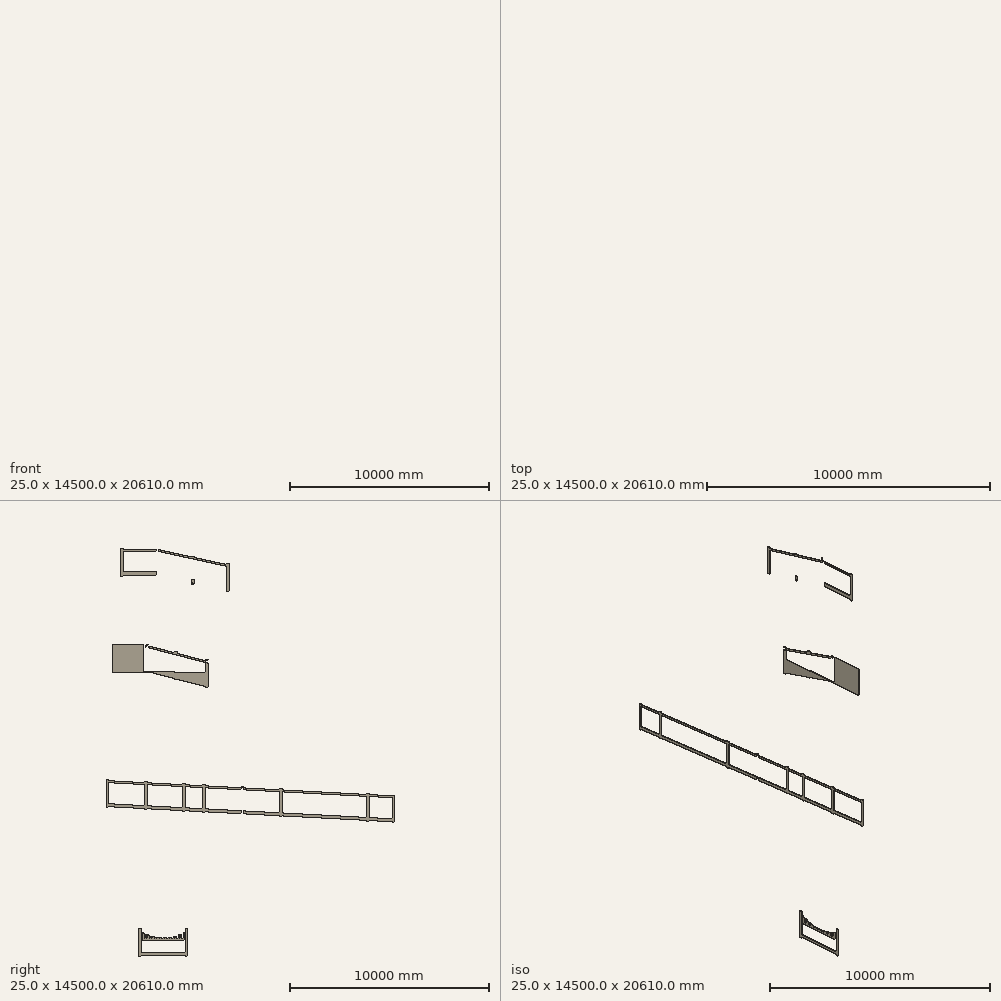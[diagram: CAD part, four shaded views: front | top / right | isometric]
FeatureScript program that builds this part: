
annotation { "Feature Type Name" : "Feature", "Feature Type Description" : "" }
export const myFeature = defineFeature(function(context is Context, id is Id, definition is map)
    precondition{}
    {
        {
            var Q0;
            Q0=qCreatedBy(makeId("Right.planeOp"),FACE);
            var sketch = newSketch(context, id + "F0", { "sketchPlane" : qUnion([Q0])});
            skLineSegment(sketch, "E0", {"start": v(-1036.7, 0) * mm, "end": v(-909.7, 0) * mm});
            skLineSegment(sketch, "E1.top", {"start": v(-1036.7, 1400) * mm, "end": v(-909.7, 1400) * mm});
            skLineSegment(sketch, "E1.left", {"start": v(-1036.7, 0) * mm, "end": v(-1036.7, 1400) * mm});
            skLineSegment(sketch, "E1.right", {"start": v(-909.7, 0) * mm, "end": v(-909.7, 1400) * mm});
            skLineSegment(sketch, "E2", {"start": v(4423.3, 650) * mm, "end": v(4423.3, -750) * mm});
            skLineSegment(sketch, "E3", {"start": v(4423.3, -750) * mm, "end": v(4296.3, -750) * mm});
            skLineSegment(sketch, "E4", {"start": v(4296.3, -750) * mm, "end": v(4296.3, 650) * mm});
            skLineSegment(sketch, "E5", {"start": v(4296.3, 650) * mm, "end": v(4423.3, 650) * mm});
            skPoint(sketch, "E6.orphan", {"position": v(4423.3, 1400) * mm});
            skPoint(sketch, "E7.orphan", {"position": v(8746.3, 0) * mm});
            skLineSegment(sketch, "E8", {"start": v(4296.3, -700) * mm, "end": v(4296.3, -515.03) * mm});
            skLineSegment(sketch, "E9.trimOffspring", {"start": v(4296.3, 0) * mm, "end": v(4423.3, 0) * mm});
            skLineSegment(sketch, "E10", {"start": v(740.8, 1183.99) * mm, "end": v(740.8, 0) * mm});
            skLineSegment(sketch, "E11", {"start": v(867.8, 0) * mm, "end": v(867.8, 1183.99) * mm});
            skLineSegment(sketch, "E12", {"start": v(2518.3, 1009.98) * mm, "end": v(2518.3, -390.02) * mm});
            skLineSegment(sketch, "E13", {"start": v(2518.3, -390.02) * mm, "end": v(2645.3, -390.02) * mm});
            skLineSegment(sketch, "E14", {"start": v(2645.3, -390.02) * mm, "end": v(2645.3, 1009.98) * mm});
            skLineSegment(sketch, "E15", {"start": v(2645.3, 1009.98) * mm, "end": v(2518.3, 1009.98) * mm});
            skLineSegment(sketch, "E16", {"start": v(-1450.3, -4815.22) * mm, "end": v(3379.7, -4815.22) * mm});
            skLineSegment(sketch, "E17", {"start": v(-1450.3, -3415.22) * mm, "end": v(-1450.3, -4815.22) * mm});
            skLineSegment(sketch, "E18", {"start": v(-1295.9, -4815.22) * mm, "end": v(-1295.9, -3415.22) * mm});
            skLineSegment(sketch, "E19", {"start": v(-1295.9, -3415.22) * mm, "end": v(-1450.3, -3415.22) * mm});
            skLineSegment(sketch, "E20.1.0.0", {"start": v(265.98, -4815.22) * mm, "end": v(265.98, -3415.7) * mm});
            skLineSegment(sketch, "E20.1.0.1", {"start": v(109.7, -3415.7) * mm, "end": v(109.7, -4815.22) * mm});
            skLineSegment(sketch, "E20.1.0.2", {"start": v(265.98, -3415.7) * mm, "end": v(109.7, -3415.7) * mm});
            skLineSegment(sketch, "E20.2.0.0", {"start": v(1824.1, -5179) * mm, "end": v(1824.1, -3779) * mm});
            skLineSegment(sketch, "E20.2.0.1", {"start": v(1671.6, -3779) * mm, "end": v(1671.6, -5179) * mm});
            skLineSegment(sketch, "E20.2.0.2", {"start": v(1824.1, -3407.94) * mm, "end": v(1671.6, -3407.94) * mm});
            skLineSegment(sketch, "E20.3.0.0", {"start": v(3384.1, -5585.22) * mm, "end": v(3384.1, -4185.22) * mm});
            skLineSegment(sketch, "E20.3.0.1", {"start": v(3229.7, -4185.22) * mm, "end": v(3229.7, -5585.22) * mm});
            skLineSegment(sketch, "E20.3.0.2", {"start": v(3384.1, -3415.22) * mm, "end": v(3229.7, -3415.22) * mm});
            skLineSegment(sketch, "E21", {"start": v(3229.7, -5585.22) * mm, "end": v(3384.1, -5585.22) * mm});
            skLineSegment(sketch, "E22", {"start": v(-1295.9, -3415.22) * mm, "end": v(5420.8, -3415.22) * mm});
            skLineSegment(sketch, "E23", {"start": v(3384.1, -4185.22) * mm, "end": v(3229.7, -4185.22) * mm});
            skLineSegment(sketch, "E24", {"start": v(1671.6, -3779) * mm, "end": v(1824.1, -3779) * mm});
            skLineSegment(sketch, "E25", {"start": v(109.7, -3465.7) * mm, "end": v(265.98, -3465.7) * mm});
            skLineSegment(sketch, "E26", {"start": v(3229.7, -4235.22) * mm, "end": v(3384.1, -4235.22) * mm});
            skLineSegment(sketch, "E27", {"start": v(-1450.3, -3465.22) * mm, "end": v(-1295.9, -3465.22) * mm});
            skPoint(sketch, "E28.orphan", {"position": v(0, -3465.7) * mm});
            skLineSegment(sketch, "E29", {"start": v(265.98, -3465.7) * mm, "end": v(3229.7, -4235.22) * mm});
            skLineSegment(sketch, "E30", {"start": v(1671.6, -5179) * mm, "end": v(1824.1, -5179) * mm});
            skLineSegment(sketch, "E31", {"start": v(-1450.3, -4765.22) * mm, "end": v(3379.7, -4765.22) * mm});
            skLineSegment(sketch, "E32", {"start": v(265.98, -4765.22) * mm, "end": v(3229.7, -5535.22) * mm});
            skLineSegment(sketch, "E33", {"start": v(740.8, 1183.99) * mm, "end": v(740.8, 1400) * mm});
            skLineSegment(sketch, "E34", {"start": v(740.8, 1400) * mm, "end": v(867.8, 1400) * mm});
            skLineSegment(sketch, "E35", {"start": v(867.8, 1400) * mm, "end": v(867.8, 1183.99) * mm});
            skLineSegment(sketch, "E36", {"start": v(-909.7, 1350) * mm, "end": v(740.8, 1350) * mm});
            skLineSegment(sketch, "E37", {"start": v(740.8, 1350) * mm, "end": v(740.8, 1261.25) * mm});
            skLineSegment(sketch, "E38", {"start": v(740.8, 1261.25) * mm, "end": v(-909.7, 1261.25) * mm});
            skLineSegment(sketch, "E39", {"start": v(867.8, 1350) * mm, "end": v(4296.3, 600) * mm});
            skLineSegment(sketch, "E40", {"start": v(4296.3, 511.25) * mm, "end": v(867.8, 1261.25) * mm});
            skLineSegment(sketch, "E41", {"start": v(-909.7, 234.97) * mm, "end": v(740.8, 234.97) * mm});
            skLineSegment(sketch, "E42", {"start": v(740.8, 234.97) * mm, "end": v(740.8, 50) * mm});
            skLineSegment(sketch, "E43", {"start": v(740.8, 50) * mm, "end": v(-909.7, 50) * mm});
            skLineSegment(sketch, "E44", {"start": v(4296.3, -700) * mm, "end": v(867.8, 50) * mm});
            skLineSegment(sketch, "E45", {"start": v(867.8, 50) * mm, "end": v(867.8, 234.97) * mm});
            skLineSegment(sketch, "E46", {"start": v(867.8, 234.97) * mm, "end": v(4296.3, -515.03) * mm});
            skLineSegment(sketch, "E47", {"start": v(740.8, 0) * mm, "end": v(867.8, 0) * mm});
            skLineSegment(sketch, "E48.trimOffspring", {"start": v(867.8, 1400) * mm, "end": v(740.8, 1400) * mm});
            skPoint(sketch, "E49.start.orphan", {"position": v(5203.57, 1400) * mm});
            skPoint(sketch, "E50.trimOffspring.end.orphan", {"position": v(2518.3, 1400) * mm});
            skLineSegment(sketch, "E51", {"start": v(936.62, 219.92) * mm, "end": v(936.62, 1511.5) * mm});
            skLineSegment(sketch, "E52", {"start": v(936.62, 1511.5) * mm, "end": v(974.62, 1511.5) * mm});
            skLineSegment(sketch, "E53", {"start": v(974.62, 1511.5) * mm, "end": v(974.62, 127.15) * mm});
            skLineSegment(sketch, "E54", {"start": v(974.62, 127.15) * mm, "end": v(936.62, 127.15) * mm});
            skLineSegment(sketch, "E55", {"start": v(936.62, 127.15) * mm, "end": v(936.62, 219.92) * mm});
            skLineSegment(sketch, "E56", {"start": v(964.44, 213.83) * mm, "end": v(986.75, 208.95) * mm});
            skLineSegment(sketch, "E57", {"start": v(867.8, 234.97) * mm, "end": v(6462.55, 234.97) * mm});
            skLineSegment(sketch, "E58", {"start": v(2645.3, -153.86) * mm, "end": v(6982.64, -153.86) * mm});
            skLineSegment(sketch, "E59", {"start": v(-1767.52, -11612.14) * mm, "end": v(-1640.52, -11612.14) * mm});
            skLineSegment(sketch, "E60", {"start": v(12732.48, -12382.14) * mm, "end": v(12732.48, -11612.14) * mm});
            skLineSegment(sketch, "E61", {"start": v(12732.48, -12382.14) * mm, "end": v(12605.48, -12375.4) * mm});
            skLineSegment(sketch, "E62", {"start": v(-1767.52, -11612.14) * mm, "end": v(-1767.52, -10212.14) * mm});
            skLineSegment(sketch, "E63", {"start": v(-1767.52, -10212.14) * mm, "end": v(-1640.52, -10212.14) * mm});
            skLineSegment(sketch, "E64", {"start": v(-1640.52, -10212.14) * mm, "end": v(-1640.52, -10262.14) * mm});
            skLineSegment(sketch, "E65", {"start": v(-1640.52, -11568.81) * mm, "end": v(162.48, -11664.56) * mm});
            skLineSegment(sketch, "E66", {"start": v(12732.48, -12382.14) * mm, "end": v(12732.48, -10982.14) * mm});
            skLineSegment(sketch, "E67", {"start": v(12732.48, -10982.14) * mm, "end": v(12605.48, -10982.14) * mm});
            skLineSegment(sketch, "E68", {"start": v(12605.48, -10982.14) * mm, "end": v(12605.48, -11018.65) * mm});
            skLineSegment(sketch, "E69", {"start": v(-1640.52, -10262.14) * mm, "end": v(162.48, -10357.88) * mm});
            skLineSegment(sketch, "E70.bottom", {"start": v(162.48, -10314.63) * mm, "end": v(289.48, -10314.63) * mm});
            skLineSegment(sketch, "E70.top", {"start": v(162.48, -11714.63) * mm, "end": v(289.48, -11714.63) * mm});
            skLineSegment(sketch, "E70.left", {"start": v(162.48, -10314.63) * mm, "end": v(162.48, -11714.63) * mm});
            skLineSegment(sketch, "E70.right", {"start": v(289.48, -10314.63) * mm, "end": v(289.48, -11714.63) * mm});
            skLineSegment(sketch, "E71.2.0.0", {"start": v(11312.48, -10896.15) * mm, "end": v(11312.48, -12296.15) * mm});
            skLineSegment(sketch, "E71.2.0.1", {"start": v(11439.48, -10896.15) * mm, "end": v(11439.48, -12296.15) * mm});
            skLineSegment(sketch, "E71.2.0.2", {"start": v(11312.48, -12296.15) * mm, "end": v(11439.48, -12296.15) * mm});
            skLineSegment(sketch, "E71.2.0.3", {"start": v(11312.48, -10896.15) * mm, "end": v(11439.48, -10896.15) * mm});
            skLineSegment(sketch, "E72.bottom", {"start": v(2075.48, -10401.68) * mm, "end": v(2202.48, -10401.68) * mm});
            skLineSegment(sketch, "E72.top", {"start": v(2075.48, -11801.68) * mm, "end": v(2202.48, -11801.68) * mm});
            skLineSegment(sketch, "E72.left", {"start": v(2075.48, -10401.68) * mm, "end": v(2075.48, -11801.68) * mm});
            skLineSegment(sketch, "E72.right", {"start": v(2202.48, -10401.68) * mm, "end": v(2202.48, -11801.68) * mm});
            skLineSegment(sketch, "E73.bottom", {"start": v(3082.48, -10447.1) * mm, "end": v(3209.48, -10447.1) * mm});
            skLineSegment(sketch, "E73.top", {"start": v(3082.48, -11847.1) * mm, "end": v(3209.48, -11847.1) * mm});
            skLineSegment(sketch, "E73.left", {"start": v(3082.48, -10447.1) * mm, "end": v(3082.48, -11847.1) * mm});
            skLineSegment(sketch, "E73.right", {"start": v(3209.48, -10447.1) * mm, "end": v(3209.48, -11847.1) * mm});
            skLineSegment(sketch, "E74.bottom", {"start": v(6942.48, -10674.67) * mm, "end": v(7069.48, -10674.67) * mm});
            skLineSegment(sketch, "E74.top", {"start": v(6942.48, -12074.67) * mm, "end": v(7069.48, -12074.67) * mm});
            skLineSegment(sketch, "E74.left", {"start": v(6942.48, -10674.67) * mm, "end": v(6942.48, -12074.67) * mm});
            skLineSegment(sketch, "E74.right", {"start": v(7069.48, -10674.67) * mm, "end": v(7069.48, -12074.67) * mm});
            skLineSegment(sketch, "E75.bottom", {"start": v(5012.48, -10552.15) * mm, "end": v(5139.48, -10552.15) * mm});
            skLineSegment(sketch, "E75.top", {"start": v(5012.48, -11952.15) * mm, "end": v(5139.48, -11952.15) * mm});
            skLineSegment(sketch, "E75.left", {"start": v(5012.48, -10552.15) * mm, "end": v(5012.48, -11952.15) * mm});
            skLineSegment(sketch, "E75.right", {"start": v(5139.48, -10552.15) * mm, "end": v(5139.48, -11952.15) * mm});
            skLineSegment(sketch, "E76", {"start": v(-1640.52, -10361.17) * mm, "end": v(162.48, -10456.91) * mm});
            skLineSegment(sketch, "E77", {"start": v(-1640.52, -11418.6) * mm, "end": v(162.48, -11514.35) * mm});
            skLineSegment(sketch, "E78.trimOffspring", {"start": v(-1640.52, -11618.88) * mm, "end": v(-1767.52, -11612.14) * mm});
            skLineSegment(sketch, "E79.trimOffspring", {"start": v(12605.48, -12325.32) * mm, "end": v(12605.48, -12375.4) * mm});
            skLineSegment(sketch, "E80.trimOffspring", {"start": v(12605.48, -11117.68) * mm, "end": v(12605.48, -12175.11) * mm});
            skLineSegment(sketch, "E81.trimOffspring", {"start": v(11439.48, -12263.4) * mm, "end": v(12605.48, -12325.32) * mm});
            skLineSegment(sketch, "E82.trimOffspring", {"start": v(11439.48, -12113.2) * mm, "end": v(12605.48, -12175.11) * mm});
            skLineSegment(sketch, "E83.trimOffspring", {"start": v(11439.48, -10956.73) * mm, "end": v(12605.48, -11018.65) * mm});
            skLineSegment(sketch, "E84.trimOffspring", {"start": v(11439.48, -11055.76) * mm, "end": v(12605.48, -11117.68) * mm});
            skLineSegment(sketch, "E85.trimOffspring", {"start": v(7069.48, -10823.7) * mm, "end": v(11312.48, -11049.02) * mm});
            skLineSegment(sketch, "E86.trimOffspring", {"start": v(7069.48, -10724.67) * mm, "end": v(11312.48, -10949.99) * mm});
            skLineSegment(sketch, "E87.trimOffspring", {"start": v(7069.48, -11881.13) * mm, "end": v(11312.48, -12106.45) * mm});
            skLineSegment(sketch, "E88.trimOffspring", {"start": v(7069.48, -12031.34) * mm, "end": v(11312.48, -12256.66) * mm});
            skLineSegment(sketch, "E89.trimOffspring", {"start": v(5139.48, -11928.85) * mm, "end": v(6942.48, -12024.6) * mm});
            skLineSegment(sketch, "E90.trimOffspring", {"start": v(5139.48, -11778.64) * mm, "end": v(6942.48, -11874.39) * mm});
            skLineSegment(sketch, "E91.trimOffspring", {"start": v(5139.48, -10721.21) * mm, "end": v(6942.48, -10816.96) * mm});
            skLineSegment(sketch, "E92.trimOffspring", {"start": v(5139.48, -10622.18) * mm, "end": v(6942.48, -10717.93) * mm});
            skLineSegment(sketch, "E93.trimOffspring", {"start": v(2202.48, -10466.22) * mm, "end": v(5012.48, -10615.44) * mm});
            skLineSegment(sketch, "E94.trimOffspring", {"start": v(2202.48, -10565.25) * mm, "end": v(5012.48, -10714.47) * mm});
            skLineSegment(sketch, "E95.trimOffspring", {"start": v(2202.48, -11622.68) * mm, "end": v(5012.48, -11771.9) * mm});
            skLineSegment(sketch, "E96.trimOffspring", {"start": v(2202.48, -11772.89) * mm, "end": v(5012.48, -11922.1) * mm});
            skLineSegment(sketch, "E97.trimOffspring", {"start": v(289.48, -11671.3) * mm, "end": v(2075.48, -11766.14) * mm});
            skLineSegment(sketch, "E98.trimOffspring", {"start": v(289.48, -11521.1) * mm, "end": v(2075.48, -11615.93) * mm});
            skLineSegment(sketch, "E99.trimOffspring", {"start": v(289.48, -10364.63) * mm, "end": v(2075.48, -10459.47) * mm});
            skLineSegment(sketch, "E100.trimOffspring", {"start": v(289.48, -10463.66) * mm, "end": v(2075.48, -10558.5) * mm});
            skLineSegment(sketch, "E101.trimOffspring", {"start": v(-1640.52, -10361.17) * mm, "end": v(-1640.52, -11418.6) * mm});
            skLineSegment(sketch, "E102.trimOffspring", {"start": v(-1640.52, -11568.81) * mm, "end": v(-1640.52, -11618.88) * mm});
            skLineSegment(sketch, "E103.left", {"start": v(0, -17698.55) * mm, "end": v(0, -19098.55) * mm});
            skLineSegment(sketch, "E103.right", {"start": v(2213, -17698.55) * mm, "end": v(2213, -19098.55) * mm});
            skLineSegment(sketch, "E104", {"start": v(2213, -17698.55) * mm, "end": v(2340, -17698.55) * mm});
            skLineSegment(sketch, "E105", {"start": v(2340, -17698.55) * mm, "end": v(2340, -19098.55) * mm});
            skLineSegment(sketch, "E106", {"start": v(2340, -19098.55) * mm, "end": v(2213, -19098.55) * mm});
            skLineSegment(sketch, "E107", {"start": v(0, -17698.55) * mm, "end": v(-127, -17698.55) * mm});
            skLineSegment(sketch, "E108", {"start": v(-127, -17698.55) * mm, "end": v(-127, -19098.55) * mm});
            skLineSegment(sketch, "E109", {"start": v(-127, -19098.55) * mm, "end": v(0, -19098.55) * mm});
            skLineSegment(sketch, "E110", {"start": v(0, -18198.55) * mm, "end": v(2213, -18198.55) * mm});
            skLineSegment(sketch, "E111", {"start": v(2213, -18198.55) * mm, "end": v(2213, -18286.55) * mm});
            skLineSegment(sketch, "E112", {"start": v(2213, -18286.55) * mm, "end": v(0, -18286.55) * mm});
            skLineSegment(sketch, "E113", {"start": v(0, -18286.55) * mm, "end": v(0, -18198.55) * mm});
            skLineSegment(sketch, "E114", {"start": v(0, -19048.55) * mm, "end": v(2213, -19048.55) * mm});
            skLineSegment(sketch, "E115", {"start": v(2213, -19048.55) * mm, "end": v(2213.03, -18898.55) * mm});
            skLineSegment(sketch, "E116", {"start": v(2213.03, -18898.55) * mm, "end": v(0, -18898.55) * mm});
            skLineSegment(sketch, "E117", {"start": v(45, -18898.55) * mm, "end": v(45, -17898.55) * mm});
            skLineSegment(sketch, "E118", {"start": v(45, -17898.55) * mm, "end": v(83, -17898.55) * mm});
            skLineSegment(sketch, "E119", {"start": v(83, -17898.55) * mm, "end": v(83, -18898.55) * mm});
            skLineSegment(sketch, "E120", {"start": v(83, -18898.55) * mm, "end": v(45, -18898.55) * mm});
            skPoint(sketch, "E121.startSnap0", {"position": v(1106.5, -18198.55) * mm});
            skLineSegment(sketch, "E122.1.0.0", {"start": v(166.37, -17941.55) * mm, "end": v(166.37, -18898.55) * mm});
            skLineSegment(sketch, "E122.1.0.1", {"start": v(128.37, -17898.55) * mm, "end": v(166.37, -17898.55) * mm});
            skLineSegment(sketch, "E122.1.0.2", {"start": v(128.37, -18898.55) * mm, "end": v(128.37, -17898.55) * mm});
            skLineSegment(sketch, "E122.1.0.3", {"start": v(166.37, -18898.55) * mm, "end": v(128.37, -18898.55) * mm});
            skLineSegment(sketch, "E122.2.0.0", {"start": v(249.74, -17980.07) * mm, "end": v(249.74, -18898.55) * mm});
            skLineSegment(sketch, "E122.2.0.1", {"start": v(211.74, -17898.55) * mm, "end": v(249.74, -17898.55) * mm});
            skLineSegment(sketch, "E122.2.0.2", {"start": v(211.74, -18898.55) * mm, "end": v(211.74, -17898.55) * mm});
            skLineSegment(sketch, "E122.2.0.3", {"start": v(249.74, -18898.55) * mm, "end": v(211.74, -18898.55) * mm});
            skLineSegment(sketch, "E122.3.0.0", {"start": v(333.1, -18014.37) * mm, "end": v(333.11, -18898.55) * mm});
            skLineSegment(sketch, "E122.3.0.1", {"start": v(295.1, -17898.55) * mm, "end": v(333.1, -17898.55) * mm});
            skLineSegment(sketch, "E122.3.0.2", {"start": v(295.11, -18898.55) * mm, "end": v(295.1, -17898.55) * mm});
            skLineSegment(sketch, "E122.3.0.3", {"start": v(333.11, -18898.55) * mm, "end": v(295.11, -18898.55) * mm});
            skLineSegment(sketch, "E122.4.0.0", {"start": v(416.48, -18044.67) * mm, "end": v(416.48, -18898.55) * mm});
            skLineSegment(sketch, "E122.4.0.1", {"start": v(378.48, -17898.55) * mm, "end": v(416.48, -17898.55) * mm});
            skLineSegment(sketch, "E122.4.0.2", {"start": v(378.48, -18898.55) * mm, "end": v(378.48, -17898.55) * mm});
            skLineSegment(sketch, "E122.4.0.3", {"start": v(416.48, -18898.55) * mm, "end": v(378.48, -18898.55) * mm});
            skLineSegment(sketch, "E122.5.0.0", {"start": v(499.85, -18071.14) * mm, "end": v(499.85, -18898.55) * mm});
            skLineSegment(sketch, "E122.5.0.1", {"start": v(461.85, -17898.55) * mm, "end": v(499.85, -17898.55) * mm});
            skLineSegment(sketch, "E122.5.0.2", {"start": v(461.85, -18898.55) * mm, "end": v(461.85, -17898.55) * mm});
            skLineSegment(sketch, "E122.5.0.3", {"start": v(499.85, -18898.55) * mm, "end": v(461.85, -18898.55) * mm});
            skLineSegment(sketch, "E122.6.0.0", {"start": v(583.22, -18093.93) * mm, "end": v(583.22, -18898.55) * mm});
            skLineSegment(sketch, "E122.6.0.1", {"start": v(545.22, -17898.55) * mm, "end": v(583.22, -17898.55) * mm});
            skLineSegment(sketch, "E122.6.0.2", {"start": v(545.22, -18898.55) * mm, "end": v(545.22, -17898.55) * mm});
            skLineSegment(sketch, "E122.6.0.3", {"start": v(583.22, -18898.55) * mm, "end": v(545.22, -18898.55) * mm});
            skLineSegment(sketch, "E122.7.0.0", {"start": v(666.6, -18113.16) * mm, "end": v(666.6, -18898.55) * mm});
            skLineSegment(sketch, "E122.7.0.1", {"start": v(628.6, -17898.55) * mm, "end": v(666.59, -17898.55) * mm});
            skLineSegment(sketch, "E122.7.0.2", {"start": v(628.6, -18898.55) * mm, "end": v(628.6, -17898.55) * mm});
            skLineSegment(sketch, "E122.7.0.3", {"start": v(666.6, -18898.55) * mm, "end": v(628.6, -18898.55) * mm});
            skLineSegment(sketch, "E122.8.0.0", {"start": v(749.96, -18128.93) * mm, "end": v(749.96, -18898.55) * mm});
            skLineSegment(sketch, "E122.8.0.1", {"start": v(711.96, -17898.55) * mm, "end": v(749.96, -17898.55) * mm});
            skLineSegment(sketch, "E122.8.0.2", {"start": v(711.96, -18898.55) * mm, "end": v(711.96, -17898.55) * mm});
            skLineSegment(sketch, "E122.8.0.3", {"start": v(749.96, -18898.55) * mm, "end": v(711.96, -18898.55) * mm});
            skLineSegment(sketch, "E122.9.0.0", {"start": v(833.33, -18141.3) * mm, "end": v(833.33, -18898.55) * mm});
            skLineSegment(sketch, "E122.9.0.1", {"start": v(795.33, -17898.55) * mm, "end": v(833.33, -17898.55) * mm});
            skLineSegment(sketch, "E122.9.0.2", {"start": v(795.33, -18898.55) * mm, "end": v(795.33, -17898.55) * mm});
            skLineSegment(sketch, "E122.9.0.3", {"start": v(833.33, -18898.55) * mm, "end": v(795.33, -18898.55) * mm});
            skLineSegment(sketch, "E122.10.0.0", {"start": v(916.7, -18150.36) * mm, "end": v(916.7, -18898.55) * mm});
            skLineSegment(sketch, "E122.10.0.1", {"start": v(878.7, -17898.55) * mm, "end": v(916.7, -17898.55) * mm});
            skLineSegment(sketch, "E122.10.0.2", {"start": v(878.7, -18898.55) * mm, "end": v(878.7, -17898.55) * mm});
            skLineSegment(sketch, "E122.10.0.3", {"start": v(916.7, -18898.55) * mm, "end": v(878.7, -18898.55) * mm});
            skLineSegment(sketch, "E122.11.0.0", {"start": v(1000.07, -18156.13) * mm, "end": v(1000.07, -18898.55) * mm});
            skLineSegment(sketch, "E122.11.0.1", {"start": v(962.07, -17898.55) * mm, "end": v(1000.07, -17898.55) * mm});
            skLineSegment(sketch, "E122.11.0.2", {"start": v(962.07, -18898.55) * mm, "end": v(962.07, -17898.55) * mm});
            skLineSegment(sketch, "E122.11.0.3", {"start": v(1000.07, -18898.55) * mm, "end": v(962.07, -18898.55) * mm});
            skLineSegment(sketch, "E122.12.0.0", {"start": v(1083.44, -18158.63) * mm, "end": v(1083.44, -18898.55) * mm});
            skLineSegment(sketch, "E122.12.0.1", {"start": v(1045.44, -17898.55) * mm, "end": v(1083.44, -17898.55) * mm});
            skLineSegment(sketch, "E122.12.0.2", {"start": v(1045.44, -18898.55) * mm, "end": v(1045.44, -18157.9) * mm});
            skLineSegment(sketch, "E122.12.0.3", {"start": v(1083.44, -18898.55) * mm, "end": v(1045.44, -18898.55) * mm});
            skLineSegment(sketch, "E122.13.0.0", {"start": v(1166.8, -17898.55) * mm, "end": v(1166.81, -18898.55) * mm});
            skLineSegment(sketch, "E122.13.0.1", {"start": v(1128.8, -17898.55) * mm, "end": v(1166.8, -17898.55) * mm});
            skLineSegment(sketch, "E122.13.0.2", {"start": v(1128.81, -18898.55) * mm, "end": v(1128.81, -18158.63) * mm});
            skLineSegment(sketch, "E122.13.0.3", {"start": v(1166.81, -18898.55) * mm, "end": v(1128.81, -18898.55) * mm});
            skLineSegment(sketch, "E122.14.0.0", {"start": v(1250.18, -18153.9) * mm, "end": v(1250.18, -18898.55) * mm});
            skLineSegment(sketch, "E122.14.0.1", {"start": v(1212.18, -17898.55) * mm, "end": v(1250.18, -17898.55) * mm});
            skLineSegment(sketch, "E122.14.0.2", {"start": v(1212.18, -18898.55) * mm, "end": v(1212.18, -18156.13) * mm});
            skLineSegment(sketch, "E122.14.0.3", {"start": v(1250.18, -18898.55) * mm, "end": v(1212.18, -18898.55) * mm});
            skLineSegment(sketch, "E122.15.0.0", {"start": v(1333.55, -18146.64) * mm, "end": v(1333.55, -18898.55) * mm});
            skLineSegment(sketch, "E122.15.0.1", {"start": v(1295.55, -17898.55) * mm, "end": v(1333.55, -17898.55) * mm});
            skLineSegment(sketch, "E122.15.0.2", {"start": v(1295.55, -18898.55) * mm, "end": v(1295.55, -18150.36) * mm});
            skLineSegment(sketch, "E122.15.0.3", {"start": v(1333.55, -18898.55) * mm, "end": v(1295.55, -18898.55) * mm});
            skLineSegment(sketch, "E122.16.0.0", {"start": v(1416.92, -18136.08) * mm, "end": v(1416.92, -18898.55) * mm});
            skLineSegment(sketch, "E122.16.0.2", {"start": v(1378.92, -18898.55) * mm, "end": v(1378.92, -18141.3) * mm});
            skLineSegment(sketch, "E122.16.0.3", {"start": v(1416.92, -18898.55) * mm, "end": v(1378.92, -18898.55) * mm});
            skLineSegment(sketch, "E122.17.0.0", {"start": v(1500.3, -18122.17) * mm, "end": v(1500.3, -18898.55) * mm});
            skLineSegment(sketch, "E122.17.0.2", {"start": v(1462.3, -18898.55) * mm, "end": v(1462.3, -18128.93) * mm});
            skLineSegment(sketch, "E122.17.0.3", {"start": v(1500.3, -18898.55) * mm, "end": v(1462.3, -18898.55) * mm});
            skLineSegment(sketch, "E122.18.0.0", {"start": v(1583.66, -18104.83) * mm, "end": v(1583.66, -18898.55) * mm});
            skLineSegment(sketch, "E122.18.0.2", {"start": v(1545.66, -18898.55) * mm, "end": v(1545.66, -18113.16) * mm});
            skLineSegment(sketch, "E122.18.0.3", {"start": v(1583.66, -18898.55) * mm, "end": v(1545.66, -18898.55) * mm});
            skLineSegment(sketch, "E122.19.0.0", {"start": v(1667.03, -18084) * mm, "end": v(1667.03, -18898.55) * mm});
            skLineSegment(sketch, "E122.19.0.2", {"start": v(1629.03, -18898.55) * mm, "end": v(1629.03, -18093.93) * mm});
            skLineSegment(sketch, "E122.19.0.3", {"start": v(1667.03, -18898.55) * mm, "end": v(1629.03, -18898.55) * mm});
            skLineSegment(sketch, "E122.20.0.0", {"start": v(1750.4, -18059.54) * mm, "end": v(1750.4, -18898.55) * mm});
            skLineSegment(sketch, "E122.20.0.2", {"start": v(1712.4, -18898.55) * mm, "end": v(1712.4, -18071.14) * mm});
            skLineSegment(sketch, "E122.20.0.3", {"start": v(1750.4, -18898.55) * mm, "end": v(1712.4, -18898.55) * mm});
            skLineSegment(sketch, "E122.21.0.0", {"start": v(1833.77, -18044.67) * mm, "end": v(1833.77, -18898.55) * mm});
            skLineSegment(sketch, "E122.21.0.2", {"start": v(1795.77, -18898.55) * mm, "end": v(1795.77, -18044.67) * mm});
            skLineSegment(sketch, "E122.21.0.3", {"start": v(1833.77, -18898.55) * mm, "end": v(1795.77, -18898.55) * mm});
            skLineSegment(sketch, "E122.22.0.0", {"start": v(1917.14, -18014.37) * mm, "end": v(1917.14, -18898.55) * mm});
            skLineSegment(sketch, "E122.22.0.2", {"start": v(1879.14, -18898.55) * mm, "end": v(1879.14, -18014.37) * mm});
            skLineSegment(sketch, "E122.22.0.3", {"start": v(1917.14, -18898.55) * mm, "end": v(1879.14, -18898.55) * mm});
            skLineSegment(sketch, "E122.23.0.0", {"start": v(2000.5, -17980.07) * mm, "end": v(2000.51, -18898.55) * mm});
            skLineSegment(sketch, "E122.23.0.2", {"start": v(1962.51, -18898.55) * mm, "end": v(1962.5, -17980.07) * mm});
            skLineSegment(sketch, "E122.23.0.3", {"start": v(2000.51, -18898.55) * mm, "end": v(1962.51, -18898.55) * mm});
            skLineSegment(sketch, "E122.24.0.0", {"start": v(2083.88, -17941.55) * mm, "end": v(2083.88, -18898.55) * mm});
            skLineSegment(sketch, "E122.24.0.2", {"start": v(2045.88, -18898.55) * mm, "end": v(2045.88, -17941.55) * mm});
            skLineSegment(sketch, "E122.24.0.3", {"start": v(2083.88, -18898.55) * mm, "end": v(2045.88, -18898.55) * mm});
            skLineSegment(sketch, "E122.25.0.0", {"start": v(2167.25, -17898.55) * mm, "end": v(2167.25, -18898.55) * mm});
            skLineSegment(sketch, "E122.25.0.1", {"start": v(2129.25, -17898.55) * mm, "end": v(2167.25, -17898.55) * mm});
            skLineSegment(sketch, "E122.25.0.2", {"start": v(2129.25, -18898.55) * mm, "end": v(2129.25, -17898.55) * mm});
            skLineSegment(sketch, "E122.25.0.3", {"start": v(2167.25, -18898.55) * mm, "end": v(2129.25, -18898.55) * mm});
            skLineSegment(sketch, "E122.direction1", {"start": v(83, -18898.55) * mm, "end": v(166.37, -18898.55) * mm, "construction": true});
            skArc(sketch, "E123", {"start": v(83, -17898.55) * mm, "mid": v(924.08, -18151) * mm, "end": v(1795.77, -18044.67) * mm});
            skPoint(sketch, "E124.orphan", {"position": v(2045.88, -17898.55) * mm});
            skPoint(sketch, "E125.orphan", {"position": v(1962.5, -17898.55) * mm});
            skPoint(sketch, "E126.orphan", {"position": v(1879.14, -17898.55) * mm});
            skPoint(sketch, "E127.orphan", {"position": v(1795.77, -17898.55) * mm});
            skPoint(sketch, "E128.orphan", {"position": v(1712.4, -17898.55) * mm});
            skPoint(sketch, "E129.orphan", {"position": v(1667.03, -17898.55) * mm});
            skPoint(sketch, "E130.orphan", {"position": v(1629.03, -17898.55) * mm});
            skPoint(sketch, "E131.orphan", {"position": v(1462.3, -17898.55) * mm});
            skLineSegment(sketch, "E132", {"start": v(2045.88, -17941.55) * mm, "end": v(2083.88, -17941.55) * mm});
            skLineSegment(sketch, "E133", {"start": v(1962.5, -17980.07) * mm, "end": v(2000.5, -17980.07) * mm});
            skLineSegment(sketch, "E134", {"start": v(1879.14, -18014.37) * mm, "end": v(1917.14, -18014.37) * mm});
            skLineSegment(sketch, "E135", {"start": v(1795.77, -18044.67) * mm, "end": v(1833.77, -18044.67) * mm});
            skLineSegment(sketch, "E136", {"start": v(1712.4, -18071.14) * mm, "end": v(1750.4, -18071.14) * mm});
            skLineSegment(sketch, "E137", {"start": v(1629.03, -18093.93) * mm, "end": v(1667.03, -18093.93) * mm});
            skLineSegment(sketch, "E138", {"start": v(1545.66, -18113.16) * mm, "end": v(1583.66, -18113.16) * mm});
            skLineSegment(sketch, "E139", {"start": v(1462.3, -18128.93) * mm, "end": v(1500.3, -18128.93) * mm});
            skLineSegment(sketch, "E140", {"start": v(1378.92, -18141.3) * mm, "end": v(1416.92, -18141.3) * mm});
            skLineSegment(sketch, "E141", {"start": v(166.37, -17941.55) * mm, "end": v(128.37, -17941.55) * mm});
            skLineSegment(sketch, "E142", {"start": v(249.74, -17980.07) * mm, "end": v(211.74, -17980.07) * mm});
            skLineSegment(sketch, "E143", {"start": v(333.1, -18014.37) * mm, "end": v(295.1, -18014.37) * mm});
            skLineSegment(sketch, "E144", {"start": v(416.48, -18044.67) * mm, "end": v(378.48, -18044.67) * mm});
            skLineSegment(sketch, "E145", {"start": v(499.85, -18071.14) * mm, "end": v(461.85, -18071.14) * mm});
            skLineSegment(sketch, "E146", {"start": v(583.22, -18093.93) * mm, "end": v(545.22, -18093.93) * mm});
            skLineSegment(sketch, "E147", {"start": v(666.6, -18113.16) * mm, "end": v(628.6, -18113.16) * mm});
            skLineSegment(sketch, "E148", {"start": v(749.96, -18128.93) * mm, "end": v(711.96, -18128.93) * mm});
            skLineSegment(sketch, "E149", {"start": v(833.33, -18141.3) * mm, "end": v(795.33, -18141.3) * mm});
            skLineSegment(sketch, "E150", {"start": v(916.7, -18150.36) * mm, "end": v(878.7, -18150.36) * mm});
            skLineSegment(sketch, "E151", {"start": v(1000.07, -18156.13) * mm, "end": v(962.07, -18156.13) * mm});
            skLineSegment(sketch, "E152", {"start": v(1083.44, -18158.63) * mm, "end": v(1045.44, -18158.63) * mm});
            skLineSegment(sketch, "E153", {"start": v(1128.81, -18158.63) * mm, "end": v(1166.8, -18158.63) * mm});
            skLineSegment(sketch, "E154", {"start": v(1212.18, -18156.13) * mm, "end": v(1250.18, -18156.13) * mm});
            skLineSegment(sketch, "E155", {"start": v(1295.55, -18150.36) * mm, "end": v(1333.55, -18150.36) * mm});
            skLineSegment(sketch, "E156", {"start": v(867.8, 1350) * mm, "end": v(804.3, 1363.9) * mm});
            skPoint(sketch, "E156.endSnap0", {"position": v(804.3, 1400) * mm});
            skLineSegment(sketch, "E157", {"start": v(804.3, 1363.9) * mm, "end": v(781.85, 1261.25) * mm});
            skLineSegment(sketch, "E158", {"start": v(1016.26, 1228.78) * mm, "end": v(645.18, 1309.95) * mm});
            skLineSegment(sketch, "E159", {"start": v(936.62, 1380.26) * mm, "end": v(936.62, 1176.06) * mm});
            skLineSegment(sketch, "E160", {"start": v(785.78, 1279.2) * mm, "end": v(936.62, 1246.2) * mm});
            skLineSegment(sketch, "E161", {"start": v(936.62, 1445.87) * mm, "end": v(936.62, 1101.6) * mm});
            skLineSegment(sketch, "E162", {"start": v(936.62, 1334.95) * mm, "end": v(804.3, 1363.9) * mm});
            skLineSegment(sketch, "E163", {"start": v(265.98, -3556.62) * mm, "end": v(3648.61, -4434.9) * mm});
            skLineSegment(sketch, "E164", {"start": v(353.37, -3488.4) * mm, "end": v(193.5, -3446.89) * mm});
            skLineSegment(sketch, "E165", {"start": v(193.5, -3446.89) * mm, "end": v(162.03, -3568.15) * mm});
            skLineSegment(sketch, "E166", {"start": v(360, -3581.03) * mm, "end": v(128.05, -3520.8) * mm});
            skLineSegment(sketch, "E167", {"start": v(336.32, -3268.84) * mm, "end": v(336.32, -3957.4) * mm});
            skLineSegment(sketch, "E168", {"start": v(336.32, -3483.97) * mm, "end": v(193.5, -3446.89) * mm});
            skLineSegment(sketch, "E169", {"start": v(336.32, -3574.89) * mm, "end": v(171.4, -3532.06) * mm});
            skLineSegment(sketch, "E170", {"start": v(2747.98, -153.86) * mm, "end": v(2221.47, -153.86) * mm});
            skLineSegment(sketch, "E171", {"start": v(2644.45, -338.65) * mm, "end": v(2213.3, -338.65) * mm});
            skLineSegment(sketch, "E172", {"start": v(2213.3, -338.65) * mm, "end": v(2985.3, -338.65) * mm});
            skLineSegment(sketch, "E173", {"start": v(2518.11, -124.56) * mm, "end": v(2809.2, -124.56) * mm});
            skLineSegment(sketch, "E174", {"start": v(2809.2, -124.56) * mm, "end": v(2270.22, -124.56) * mm});
            skLineSegment(sketch, "E175", {"start": v(5139.48, -10622.18) * mm, "end": v(4606.14, -10622.18) * mm});
            skSolve(sketch);
        }
        {
            var Q0;
            {var subQ0=sQuery(id+"F0.wireOp",EDGE,"E15");Q0=makeQuery(id+"F0.imprint","IMPRINT",FACE,{"disambiguationData":[TD([[makeQuery(id+"F0.imprint","IMPRINT",EDGE,{"derivedFrom":subQ0}),1.0]])]});}
            var Q1;
            {var subQ0=sQuery(id+"F0.wireOp",EDGE,"E13");Q1=makeQuery(id+"F0.imprint","IMPRINT",FACE,{"disambiguationData":[TD([[makeQuery(id+"F0.imprint","IMPRINT",EDGE,{"derivedFrom":subQ0}),1.0]])]});}
            var Q2;
            {var subQ0=sQuery(id+"F0.wireOp",EDGE,"E30");Q2=makeQuery(id+"F0.imprint","IMPRINT",FACE,{"disambiguationData":[TD([[makeQuery(id+"F0.imprint","IMPRINT",EDGE,{"derivedFrom":subQ0}),1.0]])]});}
            var Q3;
            {var subQ0=sQuery(id+"F0.wireOp",EDGE,"E24");Q3=makeQuery(id+"F0.imprint","IMPRINT",FACE,{"disambiguationData":[TD([[makeQuery(id+"F0.imprint","IMPRINT",EDGE,{"derivedFrom":subQ0}),-1.0]])]});}
            var Q4;
            {var subQ0=sQuery(id+"F0.wireOp",EDGE,"E23");Q4=makeQuery(id+"F0.imprint","IMPRINT",FACE,{"disambiguationData":[TD([[makeQuery(id+"F0.imprint","IMPRINT",EDGE,{"derivedFrom":subQ0}),1.0]])]});}
            var Q5;
            {var subQ5=sQuery(id+"F0.wireOp",EDGE,"E52");Q5=makeQuery(id+"F0.imprint","IMPRINT",FACE,{"disambiguationData":[TD([[makeQuery(id+"F0.imprint","IMPRINT",EDGE,{"derivedFrom":subQ5}),-1.0]])]});}
            var Q6;
            {var subQ0=sQuery(id+"F0.wireOp",EDGE,"E59");Q6=makeQuery(id+"F0.imprint","IMPRINT",FACE,{"disambiguationData":[TD([[makeQuery(id+"F0.imprint","IMPRINT",EDGE,{"derivedFrom":subQ0}),-1.0]])]});}
            var Q7;
            {var subQ0=sQuery(id+"F0.wireOp",EDGE,"E73.bottom");Q7=makeQuery(id+"F0.imprint","IMPRINT",FACE,{"disambiguationData":[TD([[makeQuery(id+"F0.imprint","IMPRINT",EDGE,{"derivedFrom":subQ0}),-1.0]])]});}
            var Q8;
            {var subQ0=sQuery(id+"F0.wireOp",EDGE,"E73.top");Q8=makeQuery(id+"F0.imprint","IMPRINT",FACE,{"disambiguationData":[TD([[makeQuery(id+"F0.imprint","IMPRINT",EDGE,{"derivedFrom":subQ0}),1.0]])]});}
            var Q9;
            {var subQ5=sQuery(id+"F0.wireOp",EDGE,"E134");Q9=makeQuery(id+"F0.imprint","IMPRINT",FACE,{"disambiguationData":[TD([[makeQuery(id+"F0.imprint","IMPRINT",EDGE,{"derivedFrom":subQ5}),-1.0]])]});}
            var Q10;
            {var subQ5=sQuery(id+"F0.wireOp",EDGE,"E133");Q10=makeQuery(id+"F0.imprint","IMPRINT",FACE,{"disambiguationData":[TD([[makeQuery(id+"F0.imprint","IMPRINT",EDGE,{"derivedFrom":subQ5}),-1.0]])]});}
            var Q11;
            {var subQ5=sQuery(id+"F0.wireOp",EDGE,"E132");Q11=makeQuery(id+"F0.imprint","IMPRINT",FACE,{"disambiguationData":[TD([[makeQuery(id+"F0.imprint","IMPRINT",EDGE,{"derivedFrom":subQ5}),-1.0]])]});}
            var Q12;
            {var subQ5=sQuery(id+"F0.wireOp",EDGE,"E122.25.0.1");Q12=makeQuery(id+"F0.imprint","IMPRINT",FACE,{"disambiguationData":[TD([[makeQuery(id+"F0.imprint","IMPRINT",EDGE,{"derivedFrom":subQ5}),-1.0]])]});}
            var Q13;
            {var subQ0=sQuery(id+"F0.wireOp",EDGE,"E17");var subQ1=sQuery(id+"F0.wireOp",EDGE,"E16");var subQ2=makeQuery(id+"F0.imprint","INTERSECT",VERTEX,{"derivedFrom":[subQ1,subQ0]});Q13=makeQuery(id+"F0.imprint","IMPRINT",FACE,{"disambiguationData":[TD([[makeQuery(id+"F0.imprint","IMPRINT",EDGE,{"disambiguationData":[TD([[subQ2,-1.0]])],"derivedFrom":subQ1}),1.0]])]});}
            var Q14;
            {var subQ0=sQuery(id+"F0.wireOp",EDGE,"E20.1.0.0");var subQ1=sQuery(id+"F0.wireOp",EDGE,"E16");var subQ2=makeQuery(id+"F0.imprint","INTERSECT",VERTEX,{"derivedFrom":[subQ1,subQ0]});Q14=makeQuery(id+"F0.imprint","IMPRINT",FACE,{"disambiguationData":[TD([[makeQuery(id+"F0.imprint","IMPRINT",EDGE,{"disambiguationData":[TD([[subQ2,-1.0]])],"derivedFrom":subQ1}),1.0]])]});}
            var Q15;
            {var subQ0=sQuery(id+"F0.wireOp",EDGE,"E32");var subQ1=sQuery(id+"F0.wireOp",EDGE,"E16");var subQ2=makeQuery(id+"F0.imprint","INTERSECT",VERTEX,{"derivedFrom":[subQ1,subQ0]});Q15=makeQuery(id+"F0.imprint","IMPRINT",FACE,{"disambiguationData":[TD([[makeQuery(id+"F0.imprint","IMPRINT",EDGE,{"disambiguationData":[TD([[subQ2,-1.0]])],"derivedFrom":subQ1}),-1.0]])]});}
            var Q16;
            {var subQ0=sQuery(id+"F0.wireOp",EDGE,"E19");Q16=makeQuery(id+"F0.imprint","IMPRINT",FACE,{"disambiguationData":[TD([[makeQuery(id+"F0.imprint","IMPRINT",EDGE,{"derivedFrom":subQ0}),1.0]])]});}
            var Q17;
            {var subQ3=sQuery(id+"F0.wireOp",EDGE,"E25");Q17=makeQuery(id+"F0.imprint","IMPRINT",FACE,{"disambiguationData":[TD([[makeQuery(id+"F0.imprint","IMPRINT",EDGE,{"derivedFrom":subQ3}),1.0]])]});}
            var Q18;
            {var subQ4=sQuery(id+"F0.wireOp",EDGE,"E61");Q18=makeQuery(id+"F0.imprint","IMPRINT",FACE,{"disambiguationData":[TD([[makeQuery(id+"F0.imprint","IMPRINT",EDGE,{"derivedFrom":subQ4}),-1.0]])]});}
            var Q19;
            {var subQ0=sQuery(id+"F0.wireOp",EDGE,"E115");Q19=makeQuery(id+"F0.imprint","IMPRINT",FACE,{"disambiguationData":[TD([[makeQuery(id+"F0.imprint","IMPRINT",EDGE,{"derivedFrom":subQ0}),1.0]])]});}
            var Q20;
            {var subQ5=sQuery(id+"F0.wireOp",EDGE,"E118");Q20=makeQuery(id+"F0.imprint","IMPRINT",FACE,{"disambiguationData":[TD([[makeQuery(id+"F0.imprint","IMPRINT",EDGE,{"derivedFrom":subQ5}),-1.0]])]});}
            var Q21;
            {var subQ5=sQuery(id+"F0.wireOp",EDGE,"E135");Q21=makeQuery(id+"F0.imprint","IMPRINT",FACE,{"disambiguationData":[TD([[makeQuery(id+"F0.imprint","IMPRINT",EDGE,{"derivedFrom":subQ5}),-1.0]])]});}
            var Q22;
            {var subQ3=sQuery(id+"F0.wireOp",EDGE,"E152");Q22=makeQuery(id+"F0.imprint","IMPRINT",FACE,{"disambiguationData":[TD([[makeQuery(id+"F0.imprint","IMPRINT",EDGE,{"derivedFrom":subQ3}),-1.0]])]});}
            var Q23;
            {var subQ0=sQuery(id+"F0.wireOp",EDGE,"E153");Q23=makeQuery(id+"F0.imprint","IMPRINT",FACE,{"disambiguationData":[TD([[makeQuery(id+"F0.imprint","IMPRINT",EDGE,{"derivedFrom":subQ0}),1.0]])]});}
            var Q24;
            {var subQ1=sQuery(id+"F0.wireOp",EDGE,"E0");Q24=makeQuery(id+"F0.imprint","IMPRINT",FACE,{"disambiguationData":[TD([[makeQuery(id+"F0.imprint","IMPRINT",EDGE,{"derivedFrom":subQ1}),1.0]])]});}
            var Q25;
            {var subQ0=sQuery(id+"F0.wireOp",EDGE,"E41");Q25=makeQuery(id+"F0.imprint","IMPRINT",FACE,{"disambiguationData":[TD([[makeQuery(id+"F0.imprint","IMPRINT",EDGE,{"derivedFrom":subQ0}),-1.0]])]});}
            var Q26;
            {var subQ0=sQuery(id+"F0.wireOp",EDGE,"E36");Q26=makeQuery(id+"F0.imprint","IMPRINT",FACE,{"disambiguationData":[TD([[makeQuery(id+"F0.imprint","IMPRINT",EDGE,{"derivedFrom":subQ0}),-1.0]])]});}
            var Q27;
            {var subQ0=sQuery(id+"F0.wireOp",EDGE,"E5");Q27=makeQuery(id+"F0.imprint","IMPRINT",FACE,{"disambiguationData":[TD([[makeQuery(id+"F0.imprint","IMPRINT",EDGE,{"derivedFrom":subQ0}),-1.0]])]});}
            var Q28;
            {var subQ0=sQuery(id+"F0.wireOp",EDGE,"E9.trimOffspring");Q28=makeQuery(id+"F0.imprint","IMPRINT",FACE,{"disambiguationData":[TD([[makeQuery(id+"F0.imprint","IMPRINT",EDGE,{"derivedFrom":subQ0}),1.0]])]});}
            var Q29;
            {var subQ0=sQuery(id+"F0.wireOp",EDGE,"E9.trimOffspring");Q29=makeQuery(id+"F0.imprint","IMPRINT",FACE,{"disambiguationData":[TD([[makeQuery(id+"F0.imprint","IMPRINT",EDGE,{"derivedFrom":subQ0}),-1.0]])]});}
            var Q30;
            {var subQ4=sQuery(id+"F0.wireOp",EDGE,"E3");Q30=makeQuery(id+"F0.imprint","IMPRINT",FACE,{"disambiguationData":[TD([[makeQuery(id+"F0.imprint","IMPRINT",EDGE,{"derivedFrom":subQ4}),-1.0]])]});}
            var Q31;
            {var subQ0=sQuery(id+"F0.wireOp",EDGE,"E39");var subQ1=sQuery(id+"F0.wireOp",EDGE,"E4");var subQ2=makeQuery(id+"F0.imprint","INTERSECT",VERTEX,{"derivedFrom":[subQ1,subQ0]});Q31=makeQuery(id+"F0.imprint","IMPRINT",FACE,{"disambiguationData":[TD([[makeQuery(id+"F0.imprint","IMPRINT",EDGE,{"disambiguationData":[TD([[subQ2,1.0]])],"derivedFrom":subQ1}),1.0]])]});}
            var Q32;
            {var subQ0=sQuery(id+"F0.wireOp",EDGE,"E8");Q32=makeQuery(id+"F0.imprint","IMPRINT",FACE,{"disambiguationData":[TD([[makeQuery(id+"F0.imprint","IMPRINT",EDGE,{"derivedFrom":subQ0}),1.0]])]});}
            var Q33;
            {var subQ0=sQuery(id+"F0.wireOp",EDGE,"E39");var subQ1=sQuery(id+"F0.wireOp",EDGE,"E12");var subQ2=makeQuery(id+"F0.imprint","INTERSECT",VERTEX,{"derivedFrom":[subQ1,subQ0]});Q33=makeQuery(id+"F0.imprint","IMPRINT",FACE,{"disambiguationData":[TD([[makeQuery(id+"F0.imprint","IMPRINT",EDGE,{"disambiguationData":[TD([[subQ2,-1.0]])],"derivedFrom":subQ1}),-1.0]])]});}
            var Q34;
            {var subQ0=sQuery(id+"F0.wireOp",EDGE,"E18");var subQ1=sQuery(id+"F0.wireOp",EDGE,"E16");var subQ2=makeQuery(id+"F0.imprint","INTERSECT",VERTEX,{"derivedFrom":[subQ1,subQ0]});Q34=makeQuery(id+"F0.imprint","IMPRINT",FACE,{"disambiguationData":[TD([[makeQuery(id+"F0.imprint","IMPRINT",EDGE,{"disambiguationData":[TD([[subQ2,-1.0]])],"derivedFrom":subQ1}),1.0]])]});}
            var Q35;
            {var subQ0=sQuery(id+"F0.wireOp",EDGE,"E20.1.0.0");var subQ1=sQuery(id+"F0.wireOp",EDGE,"E16");var subQ2=makeQuery(id+"F0.imprint","INTERSECT",VERTEX,{"derivedFrom":[subQ1,subQ0]});Q35=makeQuery(id+"F0.imprint","IMPRINT",FACE,{"disambiguationData":[TD([[makeQuery(id+"F0.imprint","IMPRINT",EDGE,{"disambiguationData":[TD([[subQ2,1.0]])],"derivedFrom":subQ1}),1.0]])]});}
            var Q36;
            {var subQ0=sQuery(id+"F0.wireOp",EDGE,"E20.3.0.1");var subQ1=sQuery(id+"F0.wireOp",EDGE,"E16");var subQ2=makeQuery(id+"F0.imprint","INTERSECT",VERTEX,{"derivedFrom":[subQ1,subQ0]});Q36=makeQuery(id+"F0.imprint","IMPRINT",FACE,{"disambiguationData":[TD([[makeQuery(id+"F0.imprint","IMPRINT",EDGE,{"disambiguationData":[TD([[subQ2,1.0]])],"derivedFrom":subQ1}),-1.0]])]});}
            var Q37;
            {var subQ0=sQuery(id+"F0.wireOp",EDGE,"E27");Q37=makeQuery(id+"F0.imprint","IMPRINT",FACE,{"disambiguationData":[TD([[makeQuery(id+"F0.imprint","IMPRINT",EDGE,{"derivedFrom":subQ0}),-1.0]])]});}
            var Q38;
            {var subQ0=sQuery(id+"F0.wireOp",EDGE,"E29");var subQ5=sQuery(id+"F0.wireOp",EDGE,"E20.2.0.1");var subQ6=makeQuery(id+"F0.imprint","INTERSECT",VERTEX,{"derivedFrom":[subQ5,subQ0]});Q38=makeQuery(id+"F0.imprint","IMPRINT",FACE,{"disambiguationData":[TD([[makeQuery(id+"F0.imprint","IMPRINT",EDGE,{"disambiguationData":[TD([[subQ6,-1.0]])],"derivedFrom":subQ5}),-1.0]])]});}
            var Q39;
            {var subQ0=sQuery(id+"F0.wireOp",EDGE,"E29");var subQ1=sQuery(id+"F0.wireOp",EDGE,"E20.2.0.0");var subQ2=makeQuery(id+"F0.imprint","INTERSECT",VERTEX,{"derivedFrom":[subQ1,subQ0]});Q39=makeQuery(id+"F0.imprint","IMPRINT",FACE,{"disambiguationData":[TD([[makeQuery(id+"F0.imprint","IMPRINT",EDGE,{"disambiguationData":[TD([[subQ2,1.0]])],"derivedFrom":subQ1}),-1.0]])]});}
            var Q40;
            {var subQ0=sQuery(id+"F0.wireOp",EDGE,"E39");var subQ1=sQuery(id+"F0.wireOp",EDGE,"E35");var subQ2=makeQuery(id+"F0.imprint","INTERSECT",VERTEX,{"derivedFrom":[subQ1,subQ0]});Q40=makeQuery(id+"F0.imprint","IMPRINT",FACE,{"disambiguationData":[TD([[makeQuery(id+"F0.imprint","IMPRINT",EDGE,{"disambiguationData":[TD([[subQ2,-1.0]])],"derivedFrom":subQ1}),1.0]])]});}
            var Q41;
            {var subQ5=sQuery(id+"F0.wireOp",EDGE,"E59");Q41=makeQuery(id+"F0.imprint","IMPRINT",FACE,{"disambiguationData":[TD([[makeQuery(id+"F0.imprint","IMPRINT",EDGE,{"derivedFrom":subQ5}),1.0]])]});}
            var Q42;
            {var subQ0=sQuery(id+"F0.wireOp",EDGE,"E99.trimOffspring");Q42=makeQuery(id+"F0.imprint","IMPRINT",FACE,{"disambiguationData":[TD([[makeQuery(id+"F0.imprint","IMPRINT",EDGE,{"derivedFrom":subQ0}),-1.0]])]});}
            var Q43;
            {var subQ0=sQuery(id+"F0.wireOp",EDGE,"E97.trimOffspring");Q43=makeQuery(id+"F0.imprint","IMPRINT",FACE,{"disambiguationData":[TD([[makeQuery(id+"F0.imprint","IMPRINT",EDGE,{"derivedFrom":subQ0}),1.0]])]});}
            var Q44;
            {var subQ0=sQuery(id+"F0.wireOp",EDGE,"E85.trimOffspring");Q44=makeQuery(id+"F0.imprint","IMPRINT",FACE,{"disambiguationData":[TD([[makeQuery(id+"F0.imprint","IMPRINT",EDGE,{"derivedFrom":subQ0}),1.0]])]});}
            var Q45;
            {var subQ0=sQuery(id+"F0.wireOp",EDGE,"E87.trimOffspring");Q45=makeQuery(id+"F0.imprint","IMPRINT",FACE,{"disambiguationData":[TD([[makeQuery(id+"F0.imprint","IMPRINT",EDGE,{"derivedFrom":subQ0}),-1.0]])]});}
            var Q46;
            {var subQ0=sQuery(id+"F0.wireOp",EDGE,"E93.trimOffspring");var subQ1=sQuery(id+"F0.wireOp",EDGE,"E72.right");var subQ2=makeQuery(id+"F0.imprint","INTERSECT",VERTEX,{"derivedFrom":[subQ1,subQ0]});Q46=makeQuery(id+"F0.imprint","IMPRINT",FACE,{"disambiguationData":[TD([[makeQuery(id+"F0.imprint","IMPRINT",EDGE,{"disambiguationData":[TD([[subQ2,-1.0]])],"derivedFrom":subQ1}),1.0]])]});}
            var Q47;
            {var subQ0=sQuery(id+"F0.wireOp",EDGE,"E95.trimOffspring");var subQ1=sQuery(id+"F0.wireOp",EDGE,"E72.right");var subQ2=makeQuery(id+"F0.imprint","INTERSECT",VERTEX,{"derivedFrom":[subQ1,subQ0]});Q47=makeQuery(id+"F0.imprint","IMPRINT",FACE,{"disambiguationData":[TD([[makeQuery(id+"F0.imprint","IMPRINT",EDGE,{"disambiguationData":[TD([[subQ2,-1.0]])],"derivedFrom":subQ1}),1.0]])]});}
            var Q48;
            {var subQ0=sQuery(id+"F0.wireOp",EDGE,"E93.trimOffspring");var subQ1=sQuery(id+"F0.wireOp",EDGE,"E73.right");var subQ2=makeQuery(id+"F0.imprint","INTERSECT",VERTEX,{"derivedFrom":[subQ1,subQ0]});Q48=makeQuery(id+"F0.imprint","IMPRINT",FACE,{"disambiguationData":[TD([[makeQuery(id+"F0.imprint","IMPRINT",EDGE,{"disambiguationData":[TD([[subQ2,-1.0]])],"derivedFrom":subQ1}),1.0]])]});}
            var Q49;
            {var subQ0=sQuery(id+"F0.wireOp",EDGE,"E96.trimOffspring");var subQ1=sQuery(id+"F0.wireOp",EDGE,"E73.right");var subQ2=makeQuery(id+"F0.imprint","INTERSECT",VERTEX,{"derivedFrom":[subQ1,subQ0]});Q49=makeQuery(id+"F0.imprint","IMPRINT",FACE,{"disambiguationData":[TD([[makeQuery(id+"F0.imprint","IMPRINT",EDGE,{"disambiguationData":[TD([[subQ2,1.0]])],"derivedFrom":subQ1}),1.0]])]});}
            var Q50;
            {var subQ0=sQuery(id+"F0.wireOp",EDGE,"E91.trimOffspring");Q50=makeQuery(id+"F0.imprint","IMPRINT",FACE,{"disambiguationData":[TD([[makeQuery(id+"F0.imprint","IMPRINT",EDGE,{"derivedFrom":subQ0}),1.0]])]});}
            var Q51;
            {var subQ0=sQuery(id+"F0.wireOp",EDGE,"E89.trimOffspring");Q51=makeQuery(id+"F0.imprint","IMPRINT",FACE,{"disambiguationData":[TD([[makeQuery(id+"F0.imprint","IMPRINT",EDGE,{"derivedFrom":subQ0}),1.0]])]});}
            var Q52;
            {var subQ5=sQuery(id+"F0.wireOp",EDGE,"E107");Q52=makeQuery(id+"F0.imprint","IMPRINT",FACE,{"disambiguationData":[TD([[makeQuery(id+"F0.imprint","IMPRINT",EDGE,{"derivedFrom":subQ5}),1.0]])]});}
            var Q53;
            {var subQ0=sQuery(id+"F0.wireOp",EDGE,"E104");Q53=makeQuery(id+"F0.imprint","IMPRINT",FACE,{"disambiguationData":[TD([[makeQuery(id+"F0.imprint","IMPRINT",EDGE,{"derivedFrom":subQ0}),-1.0]])]});}
            var Q54;
            {var subQ0=sQuery(id+"F0.wireOp",EDGE,"E122.21.0.0");var subQ1=sQuery(id+"F0.wireOp",EDGE,"E110");var subQ2=makeQuery(id+"F0.imprint","INTERSECT",VERTEX,{"derivedFrom":[subQ1,subQ0]});Q54=makeQuery(id+"F0.imprint","IMPRINT",FACE,{"disambiguationData":[TD([[makeQuery(id+"F0.imprint","IMPRINT",EDGE,{"disambiguationData":[TD([[subQ2,-1.0]])],"derivedFrom":subQ1}),-1.0]])]});}
            var Q55;
            {var subQ0=sQuery(id+"F0.wireOp",EDGE,"E122.22.0.0");var subQ1=sQuery(id+"F0.wireOp",EDGE,"E110");var subQ2=makeQuery(id+"F0.imprint","INTERSECT",VERTEX,{"derivedFrom":[subQ1,subQ0]});Q55=makeQuery(id+"F0.imprint","IMPRINT",FACE,{"disambiguationData":[TD([[makeQuery(id+"F0.imprint","IMPRINT",EDGE,{"disambiguationData":[TD([[subQ2,-1.0]])],"derivedFrom":subQ1}),-1.0]])]});}
            var Q56;
            {var subQ0=sQuery(id+"F0.wireOp",EDGE,"E122.23.0.0");var subQ1=sQuery(id+"F0.wireOp",EDGE,"E110");var subQ2=makeQuery(id+"F0.imprint","INTERSECT",VERTEX,{"derivedFrom":[subQ1,subQ0]});Q56=makeQuery(id+"F0.imprint","IMPRINT",FACE,{"disambiguationData":[TD([[makeQuery(id+"F0.imprint","IMPRINT",EDGE,{"disambiguationData":[TD([[subQ2,-1.0]])],"derivedFrom":subQ1}),-1.0]])]});}
            var Q57;
            {var subQ0=sQuery(id+"F0.wireOp",EDGE,"E122.24.0.0");var subQ1=sQuery(id+"F0.wireOp",EDGE,"E110");var subQ2=makeQuery(id+"F0.imprint","INTERSECT",VERTEX,{"derivedFrom":[subQ1,subQ0]});Q57=makeQuery(id+"F0.imprint","IMPRINT",FACE,{"disambiguationData":[TD([[makeQuery(id+"F0.imprint","IMPRINT",EDGE,{"disambiguationData":[TD([[subQ2,-1.0]])],"derivedFrom":subQ1}),-1.0]])]});}
            var Q58;
            {var subQ0=sQuery(id+"F0.wireOp",EDGE,"E111");Q58=makeQuery(id+"F0.imprint","IMPRINT",FACE,{"disambiguationData":[TD([[makeQuery(id+"F0.imprint","IMPRINT",EDGE,{"derivedFrom":subQ0}),-1.0]])]});}
            var Q59;
            {var subQ0=sQuery(id+"F0.wireOp",EDGE,"E39");var subQ1=sQuery(id+"F0.wireOp",EDGE,"E12");var subQ2=makeQuery(id+"F0.imprint","INTERSECT",VERTEX,{"derivedFrom":[subQ1,subQ0]});Q59=makeQuery(id+"F0.imprint","IMPRINT",FACE,{"disambiguationData":[TD([[makeQuery(id+"F0.imprint","IMPRINT",EDGE,{"disambiguationData":[TD([[subQ2,-1.0]])],"derivedFrom":subQ1}),1.0]])]});}
            var Q60;
            {var subQ0=sQuery(id+"F0.wireOp",EDGE,"E44");var subQ1=sQuery(id+"F0.wireOp",EDGE,"E12");var subQ2=makeQuery(id+"F0.imprint","INTERSECT",VERTEX,{"derivedFrom":[subQ1,subQ0]});Q60=makeQuery(id+"F0.imprint","IMPRINT",FACE,{"disambiguationData":[TD([[makeQuery(id+"F0.imprint","IMPRINT",EDGE,{"disambiguationData":[TD([[subQ2,1.0]])],"derivedFrom":subQ1}),1.0]])]});}
            var Q61;
            {var subQ0=sQuery(id+"F0.wireOp",EDGE,"E32");var subQ1=sQuery(id+"F0.wireOp",EDGE,"E16");var subQ2=makeQuery(id+"F0.imprint","INTERSECT",VERTEX,{"derivedFrom":[subQ1,subQ0]});Q61=makeQuery(id+"F0.imprint","IMPRINT",FACE,{"disambiguationData":[TD([[makeQuery(id+"F0.imprint","IMPRINT",EDGE,{"disambiguationData":[TD([[subQ2,-1.0]])],"derivedFrom":subQ1}),1.0]])]});}
            var Q62;
            {var subQ0=sQuery(id+"F0.wireOp",EDGE,"E20.2.0.1");var subQ1=sQuery(id+"F0.wireOp",EDGE,"E16");var subQ2=makeQuery(id+"F0.imprint","INTERSECT",VERTEX,{"derivedFrom":[subQ1,subQ0]});Q62=makeQuery(id+"F0.imprint","IMPRINT",FACE,{"disambiguationData":[TD([[makeQuery(id+"F0.imprint","IMPRINT",EDGE,{"disambiguationData":[TD([[subQ2,-1.0]])],"derivedFrom":subQ1}),-1.0]])]});}
            var Q63;
            {var subQ0=sQuery(id+"F0.wireOp",EDGE,"E25");Q63=makeQuery(id+"F0.imprint","IMPRINT",FACE,{"disambiguationData":[TD([[makeQuery(id+"F0.imprint","IMPRINT",EDGE,{"derivedFrom":subQ0}),-1.0]])]});}
            var Q64;
            {var subQ0=sQuery(id+"F0.wireOp",EDGE,"E29");var subQ1=sQuery(id+"F0.wireOp",EDGE,"E20.2.0.0");var subQ2=makeQuery(id+"F0.imprint","INTERSECT",VERTEX,{"derivedFrom":[subQ1,subQ0]});Q64=makeQuery(id+"F0.imprint","IMPRINT",FACE,{"disambiguationData":[TD([[makeQuery(id+"F0.imprint","IMPRINT",EDGE,{"disambiguationData":[TD([[subQ2,1.0]])],"derivedFrom":subQ1}),1.0]])]});}
            var Q65;
            {var subQ0=sQuery(id+"F0.wireOp",EDGE,"E21");Q65=makeQuery(id+"F0.imprint","IMPRINT",FACE,{"disambiguationData":[TD([[makeQuery(id+"F0.imprint","IMPRINT",EDGE,{"derivedFrom":subQ0}),1.0]])]});}
            var Q66;
            {var subQ0=sQuery(id+"F0.wireOp",EDGE,"E51");var subQ1=sQuery(id+"F0.wireOp",EDGE,"E39");var subQ2=makeQuery(id+"F0.imprint","INTERSECT",VERTEX,{"derivedFrom":[subQ1,subQ0]});Q66=makeQuery(id+"F0.imprint","IMPRINT",FACE,{"disambiguationData":[TD([[makeQuery(id+"F0.imprint","IMPRINT",EDGE,{"disambiguationData":[TD([[subQ2,-1.0]])],"derivedFrom":subQ1}),-1.0]])]});}
            var Q67;
            {var subQ0=sQuery(id+"F0.wireOp",EDGE,"E93.trimOffspring");var subQ1=sQuery(id+"F0.wireOp",EDGE,"E73.left");var subQ2=makeQuery(id+"F0.imprint","INTERSECT",VERTEX,{"derivedFrom":[subQ1,subQ0]});Q67=makeQuery(id+"F0.imprint","IMPRINT",FACE,{"disambiguationData":[TD([[makeQuery(id+"F0.imprint","IMPRINT",EDGE,{"disambiguationData":[TD([[subQ2,-1.0]])],"derivedFrom":subQ1}),1.0]])]});}
            var Q68;
            {var subQ0=sQuery(id+"F0.wireOp",EDGE,"E96.trimOffspring");var subQ1=sQuery(id+"F0.wireOp",EDGE,"E73.left");var subQ2=makeQuery(id+"F0.imprint","INTERSECT",VERTEX,{"derivedFrom":[subQ1,subQ0]});Q68=makeQuery(id+"F0.imprint","IMPRINT",FACE,{"disambiguationData":[TD([[makeQuery(id+"F0.imprint","IMPRINT",EDGE,{"disambiguationData":[TD([[subQ2,1.0]])],"derivedFrom":subQ1}),1.0]])]});}
            var Q69;
            {var subQ0=sQuery(id+"F0.wireOp",EDGE,"E117");var subQ1=sQuery(id+"F0.wireOp",EDGE,"E110");var subQ2=makeQuery(id+"F0.imprint","INTERSECT",VERTEX,{"derivedFrom":[subQ1,subQ0]});Q69=makeQuery(id+"F0.imprint","IMPRINT",FACE,{"disambiguationData":[TD([[makeQuery(id+"F0.imprint","IMPRINT",EDGE,{"disambiguationData":[TD([[subQ2,-1.0]])],"derivedFrom":subQ1}),-1.0]])]});}
            var Q70;
            {var subQ5=sQuery(id+"F0.wireOp",EDGE,"E141");Q70=makeQuery(id+"F0.imprint","IMPRINT",FACE,{"disambiguationData":[TD([[makeQuery(id+"F0.imprint","IMPRINT",EDGE,{"derivedFrom":subQ5}),1.0]])]});}
            var Q71;
            {var subQ5=sQuery(id+"F0.wireOp",EDGE,"E142");Q71=makeQuery(id+"F0.imprint","IMPRINT",FACE,{"disambiguationData":[TD([[makeQuery(id+"F0.imprint","IMPRINT",EDGE,{"derivedFrom":subQ5}),1.0]])]});}
            var Q72;
            {var subQ5=sQuery(id+"F0.wireOp",EDGE,"E143");Q72=makeQuery(id+"F0.imprint","IMPRINT",FACE,{"disambiguationData":[TD([[makeQuery(id+"F0.imprint","IMPRINT",EDGE,{"derivedFrom":subQ5}),1.0]])]});}
            var Q73;
            {var subQ5=sQuery(id+"F0.wireOp",EDGE,"E145");Q73=makeQuery(id+"F0.imprint","IMPRINT",FACE,{"disambiguationData":[TD([[makeQuery(id+"F0.imprint","IMPRINT",EDGE,{"derivedFrom":subQ5}),1.0]])]});}
            var Q74;
            {var subQ5=sQuery(id+"F0.wireOp",EDGE,"E146");Q74=makeQuery(id+"F0.imprint","IMPRINT",FACE,{"disambiguationData":[TD([[makeQuery(id+"F0.imprint","IMPRINT",EDGE,{"derivedFrom":subQ5}),1.0]])]});}
            var Q75;
            {var subQ5=sQuery(id+"F0.wireOp",EDGE,"E147");Q75=makeQuery(id+"F0.imprint","IMPRINT",FACE,{"disambiguationData":[TD([[makeQuery(id+"F0.imprint","IMPRINT",EDGE,{"derivedFrom":subQ5}),1.0]])]});}
            var Q76;
            {var subQ5=sQuery(id+"F0.wireOp",EDGE,"E148");Q76=makeQuery(id+"F0.imprint","IMPRINT",FACE,{"disambiguationData":[TD([[makeQuery(id+"F0.imprint","IMPRINT",EDGE,{"derivedFrom":subQ5}),1.0]])]});}
            var Q77;
            {var subQ5=sQuery(id+"F0.wireOp",EDGE,"E149");Q77=makeQuery(id+"F0.imprint","IMPRINT",FACE,{"disambiguationData":[TD([[makeQuery(id+"F0.imprint","IMPRINT",EDGE,{"derivedFrom":subQ5}),1.0]])]});}
            var Q78;
            {var subQ5=sQuery(id+"F0.wireOp",EDGE,"E150");Q78=makeQuery(id+"F0.imprint","IMPRINT",FACE,{"disambiguationData":[TD([[makeQuery(id+"F0.imprint","IMPRINT",EDGE,{"derivedFrom":subQ5}),1.0]])]});}
            var Q79;
            {var subQ5=sQuery(id+"F0.wireOp",EDGE,"E151");Q79=makeQuery(id+"F0.imprint","IMPRINT",FACE,{"disambiguationData":[TD([[makeQuery(id+"F0.imprint","IMPRINT",EDGE,{"derivedFrom":subQ5}),1.0]])]});}
            var Q80;
            {var subQ5=sQuery(id+"F0.wireOp",EDGE,"E152");Q80=makeQuery(id+"F0.imprint","IMPRINT",FACE,{"disambiguationData":[TD([[makeQuery(id+"F0.imprint","IMPRINT",EDGE,{"derivedFrom":subQ5}),1.0]])]});}
            var Q81;
            {var subQ5=sQuery(id+"F0.wireOp",EDGE,"E154");Q81=makeQuery(id+"F0.imprint","IMPRINT",FACE,{"disambiguationData":[TD([[makeQuery(id+"F0.imprint","IMPRINT",EDGE,{"derivedFrom":subQ5}),-1.0]])]});}
            var Q82;
            {var subQ5=sQuery(id+"F0.wireOp",EDGE,"E155");Q82=makeQuery(id+"F0.imprint","IMPRINT",FACE,{"disambiguationData":[TD([[makeQuery(id+"F0.imprint","IMPRINT",EDGE,{"derivedFrom":subQ5}),-1.0]])]});}
            var Q83;
            {var subQ5=sQuery(id+"F0.wireOp",EDGE,"E140");Q83=makeQuery(id+"F0.imprint","IMPRINT",FACE,{"disambiguationData":[TD([[makeQuery(id+"F0.imprint","IMPRINT",EDGE,{"derivedFrom":subQ5}),-1.0]])]});}
            var Q84;
            {var subQ5=sQuery(id+"F0.wireOp",EDGE,"E139");Q84=makeQuery(id+"F0.imprint","IMPRINT",FACE,{"disambiguationData":[TD([[makeQuery(id+"F0.imprint","IMPRINT",EDGE,{"derivedFrom":subQ5}),-1.0]])]});}
            var Q85;
            {var subQ5=sQuery(id+"F0.wireOp",EDGE,"E138");Q85=makeQuery(id+"F0.imprint","IMPRINT",FACE,{"disambiguationData":[TD([[makeQuery(id+"F0.imprint","IMPRINT",EDGE,{"derivedFrom":subQ5}),-1.0]])]});}
            var Q86;
            {var subQ5=sQuery(id+"F0.wireOp",EDGE,"E137");Q86=makeQuery(id+"F0.imprint","IMPRINT",FACE,{"disambiguationData":[TD([[makeQuery(id+"F0.imprint","IMPRINT",EDGE,{"derivedFrom":subQ5}),-1.0]])]});}
            var Q87;
            {var subQ5=sQuery(id+"F0.wireOp",EDGE,"E136");Q87=makeQuery(id+"F0.imprint","IMPRINT",FACE,{"disambiguationData":[TD([[makeQuery(id+"F0.imprint","IMPRINT",EDGE,{"derivedFrom":subQ5}),-1.0]])]});}
            var Q88;
            {var subQ0=sQuery(id+"F0.wireOp",EDGE,"E122.21.0.0");var subQ1=sQuery(id+"F0.wireOp",EDGE,"E110");var subQ2=makeQuery(id+"F0.imprint","INTERSECT",VERTEX,{"derivedFrom":[subQ1,subQ0]});Q88=makeQuery(id+"F0.imprint","IMPRINT",FACE,{"disambiguationData":[TD([[makeQuery(id+"F0.imprint","IMPRINT",EDGE,{"disambiguationData":[TD([[subQ2,1.0]])],"derivedFrom":subQ1}),-1.0]])]});}
            var Q89;
            {var subQ0=sQuery(id+"F0.wireOp",EDGE,"E122.22.0.2");var subQ1=sQuery(id+"F0.wireOp",EDGE,"E110");var subQ2=makeQuery(id+"F0.imprint","INTERSECT",VERTEX,{"derivedFrom":[subQ1,subQ0]});Q89=makeQuery(id+"F0.imprint","IMPRINT",FACE,{"disambiguationData":[TD([[makeQuery(id+"F0.imprint","IMPRINT",EDGE,{"disambiguationData":[TD([[subQ2,-1.0]])],"derivedFrom":subQ1}),-1.0]])]});}
            var Q90;
            {var subQ0=sQuery(id+"F0.wireOp",EDGE,"E122.23.0.2");var subQ1=sQuery(id+"F0.wireOp",EDGE,"E110");var subQ2=makeQuery(id+"F0.imprint","INTERSECT",VERTEX,{"derivedFrom":[subQ1,subQ0]});Q90=makeQuery(id+"F0.imprint","IMPRINT",FACE,{"disambiguationData":[TD([[makeQuery(id+"F0.imprint","IMPRINT",EDGE,{"disambiguationData":[TD([[subQ2,-1.0]])],"derivedFrom":subQ1}),-1.0]])]});}
            var Q91;
            {var subQ0=sQuery(id+"F0.wireOp",EDGE,"E122.24.0.2");var subQ1=sQuery(id+"F0.wireOp",EDGE,"E110");var subQ2=makeQuery(id+"F0.imprint","INTERSECT",VERTEX,{"derivedFrom":[subQ1,subQ0]});Q91=makeQuery(id+"F0.imprint","IMPRINT",FACE,{"disambiguationData":[TD([[makeQuery(id+"F0.imprint","IMPRINT",EDGE,{"disambiguationData":[TD([[subQ2,-1.0]])],"derivedFrom":subQ1}),-1.0]])]});}
            var Q92;
            {var subQ0=sQuery(id+"F0.wireOp",EDGE,"E122.25.0.2");var subQ1=sQuery(id+"F0.wireOp",EDGE,"E110");var subQ2=makeQuery(id+"F0.imprint","INTERSECT",VERTEX,{"derivedFrom":[subQ1,subQ0]});Q92=makeQuery(id+"F0.imprint","IMPRINT",FACE,{"disambiguationData":[TD([[makeQuery(id+"F0.imprint","IMPRINT",EDGE,{"disambiguationData":[TD([[subQ2,-1.0]])],"derivedFrom":subQ1}),-1.0]])]});}
            var Q93;
            {var subQ1=sQuery(id+"F0.wireOp",EDGE,"E45");Q93=makeQuery(id+"F0.imprint","IMPRINT",FACE,{"disambiguationData":[TD([[makeQuery(id+"F0.imprint","IMPRINT",EDGE,{"derivedFrom":subQ1}),-1.0]])]});}
            var Q94;
            {var subQ6=sQuery(id+"F0.wireOp",EDGE,"E18");var subQ9=makeQuery(id+"F0.imprint","INTERSECT",VERTEX,{"derivedFrom":[subQ6,sQuery(id+"F0.wireOp",EDGE,"E27")]});Q94=makeQuery(id+"F0.imprint","IMPRINT",FACE,{"disambiguationData":[TD([[makeQuery(id+"F0.imprint","IMPRINT",EDGE,{"disambiguationData":[TD([[subQ9,1.0]])],"derivedFrom":subQ6}),-1.0]])]});}
            var Q95;
            {var subQ4=sQuery(id+"F0.wireOp",EDGE,"E70.bottom");Q95=makeQuery(id+"F0.imprint","IMPRINT",FACE,{"disambiguationData":[TD([[makeQuery(id+"F0.imprint","IMPRINT",EDGE,{"derivedFrom":subQ4}),-1.0]])]});}
            var Q96;
            {var subQ0=sQuery(id+"F0.wireOp",EDGE,"E71.2.0.2");Q96=makeQuery(id+"F0.imprint","IMPRINT",FACE,{"disambiguationData":[TD([[makeQuery(id+"F0.imprint","IMPRINT",EDGE,{"derivedFrom":subQ0}),1.0]])]});}
            var Q97;
            {var subQ0=sQuery(id+"F0.wireOp",EDGE,"E37");Q97=makeQuery(id+"F0.imprint","IMPRINT",FACE,{"disambiguationData":[TD([[makeQuery(id+"F0.imprint","IMPRINT",EDGE,{"derivedFrom":subQ0}),1.0]])]});}
            var Q98;
            {var subQ4=sQuery(id+"F0.wireOp",EDGE,"E72.bottom");Q98=makeQuery(id+"F0.imprint","IMPRINT",FACE,{"disambiguationData":[TD([[makeQuery(id+"F0.imprint","IMPRINT",EDGE,{"derivedFrom":subQ4}),-1.0]])]});}
            var Q99;
            {var subQ4=sQuery(id+"F0.wireOp",EDGE,"E74.bottom");Q99=makeQuery(id+"F0.imprint","IMPRINT",FACE,{"disambiguationData":[TD([[makeQuery(id+"F0.imprint","IMPRINT",EDGE,{"derivedFrom":subQ4}),-1.0]])]});}
            var Q100;
            {var subQ4=sQuery(id+"F0.wireOp",EDGE,"E75.bottom");Q100=makeQuery(id+"F0.imprint","IMPRINT",FACE,{"disambiguationData":[TD([[makeQuery(id+"F0.imprint","IMPRINT",EDGE,{"derivedFrom":subQ4}),-1.0]])]});}
            var Q101;
            {var subQ25=sQuery(id+"F0.wireOp",EDGE,"E114");Q101=makeQuery(id+"F0.imprint","IMPRINT",FACE,{"disambiguationData":[TD([[makeQuery(id+"F0.imprint","IMPRINT",EDGE,{"derivedFrom":subQ25}),1.0]])]});}
            var Q102;
            {var subQ5=sQuery(id+"F0.wireOp",EDGE,"E59");Q102=makeQuery(id+"F0.imprint","IMPRINT",FACE,{"disambiguationData":[TD([[makeQuery(id+"F0.imprint","IMPRINT",EDGE,{"derivedFrom":subQ5}),1.0]])]});}
            var Q103;
            {var subQ0=sQuery(id+"F0.wireOp",EDGE,"E59");Q103=makeQuery(id+"F0.imprint","IMPRINT",FACE,{"disambiguationData":[TD([[makeQuery(id+"F0.imprint","IMPRINT",EDGE,{"derivedFrom":subQ0}),-1.0]])]});}
            var Q104;
            {var subQ5=sQuery(id+"F0.wireOp",EDGE,"E59");Q104=makeQuery(id+"F0.imprint","IMPRINT",FACE,{"disambiguationData":[TD([[makeQuery(id+"F0.imprint","IMPRINT",EDGE,{"derivedFrom":subQ5}),1.0]])]});}
            var Q105;
            {var subQ4=sQuery(id+"F0.wireOp",EDGE,"E72.bottom");Q105=makeQuery(id+"F0.imprint","IMPRINT",FACE,{"disambiguationData":[TD([[makeQuery(id+"F0.imprint","IMPRINT",EDGE,{"derivedFrom":subQ4}),-1.0]])]});}
            var Q106;
            {var subQ0=sQuery(id+"F0.wireOp",EDGE,"E59");Q106=makeQuery(id+"F0.imprint","IMPRINT",FACE,{"disambiguationData":[TD([[makeQuery(id+"F0.imprint","IMPRINT",EDGE,{"derivedFrom":subQ0}),-1.0]])]});}
            var Q107;
            {var subQ5=sQuery(id+"F0.wireOp",EDGE,"E59");Q107=makeQuery(id+"F0.imprint","IMPRINT",FACE,{"disambiguationData":[TD([[makeQuery(id+"F0.imprint","IMPRINT",EDGE,{"derivedFrom":subQ5}),1.0]])]});}
            var Q108;
            {var subQ5=sQuery(id+"F0.wireOp",EDGE,"E59");Q108=makeQuery(id+"F0.imprint","IMPRINT",FACE,{"disambiguationData":[TD([[makeQuery(id+"F0.imprint","IMPRINT",EDGE,{"derivedFrom":subQ5}),1.0]])]});}
            var Q109;
            {var subQ0=sQuery(id+"F0.wireOp",EDGE,"E59");Q109=makeQuery(id+"F0.imprint","IMPRINT",FACE,{"disambiguationData":[TD([[makeQuery(id+"F0.imprint","IMPRINT",EDGE,{"derivedFrom":subQ0}),-1.0]])]});}
            var Q110;
            {var subQ0=sQuery(id+"F0.wireOp",EDGE,"E73.top");Q110=makeQuery(id+"F0.imprint","IMPRINT",FACE,{"disambiguationData":[TD([[makeQuery(id+"F0.imprint","IMPRINT",EDGE,{"derivedFrom":subQ0}),1.0]])]});}
            var Q111;
            {var subQ0=sQuery(id+"F0.wireOp",EDGE,"E59");Q111=makeQuery(id+"F0.imprint","IMPRINT",FACE,{"disambiguationData":[TD([[makeQuery(id+"F0.imprint","IMPRINT",EDGE,{"derivedFrom":subQ0}),-1.0]])]});}
            var Q112;
            {var subQ5=sQuery(id+"F0.wireOp",EDGE,"E59");Q112=makeQuery(id+"F0.imprint","IMPRINT",FACE,{"disambiguationData":[TD([[makeQuery(id+"F0.imprint","IMPRINT",EDGE,{"derivedFrom":subQ5}),1.0]])]});}
            var Q113;
            {var subQ5=sQuery(id+"F0.wireOp",EDGE,"E59");Q113=makeQuery(id+"F0.imprint","IMPRINT",FACE,{"disambiguationData":[TD([[makeQuery(id+"F0.imprint","IMPRINT",EDGE,{"derivedFrom":subQ5}),1.0]])]});}
            var Q114;
            {var subQ0=sQuery(id+"F0.wireOp",EDGE,"E59");Q114=makeQuery(id+"F0.imprint","IMPRINT",FACE,{"disambiguationData":[TD([[makeQuery(id+"F0.imprint","IMPRINT",EDGE,{"derivedFrom":subQ0}),-1.0]])]});}
            var Q115;
            {var subQ5=sQuery(id+"F0.wireOp",EDGE,"E59");Q115=makeQuery(id+"F0.imprint","IMPRINT",FACE,{"disambiguationData":[TD([[makeQuery(id+"F0.imprint","IMPRINT",EDGE,{"derivedFrom":subQ5}),1.0]])]});}
            var Q116;
            {var subQ0=sQuery(id+"F0.wireOp",EDGE,"E59");Q116=makeQuery(id+"F0.imprint","IMPRINT",FACE,{"disambiguationData":[TD([[makeQuery(id+"F0.imprint","IMPRINT",EDGE,{"derivedFrom":subQ0}),-1.0]])]});}
            var Q117;
            {var subQ0=sQuery(id+"F0.wireOp",EDGE,"E71.2.0.2");Q117=makeQuery(id+"F0.imprint","IMPRINT",FACE,{"disambiguationData":[TD([[makeQuery(id+"F0.imprint","IMPRINT",EDGE,{"derivedFrom":subQ0}),1.0]])]});}
            var Q118;
            {var subQ0=sQuery(id+"F0.wireOp",EDGE,"E94.trimOffspring");var subQ1=sQuery(id+"F0.wireOp",EDGE,"E73.left");var subQ2=makeQuery(id+"F0.imprint","INTERSECT",VERTEX,{"derivedFrom":[subQ1,subQ0]});Q118=makeQuery(id+"F0.imprint","IMPRINT",FACE,{"disambiguationData":[TD([[makeQuery(id+"F0.imprint","IMPRINT",EDGE,{"disambiguationData":[TD([[subQ2,-1.0]])],"derivedFrom":subQ1}),1.0]])]});}
            var Q119;
            {var subQ5=sQuery(id+"F0.wireOp",EDGE,"E153");Q119=makeQuery(id+"F0.imprint","IMPRINT",FACE,{"disambiguationData":[TD([[makeQuery(id+"F0.imprint","IMPRINT",EDGE,{"derivedFrom":subQ5}),-1.0]])]});}
            var Q120;
            {var subQ0=sQuery(id+"F0.wireOp",EDGE,"E122.13.0.2");var subQ1=sQuery(id+"F0.wireOp",EDGE,"E110");var subQ2=makeQuery(id+"F0.imprint","INTERSECT",VERTEX,{"derivedFrom":[subQ1,subQ0]});Q120=makeQuery(id+"F0.imprint","IMPRINT",FACE,{"disambiguationData":[TD([[makeQuery(id+"F0.imprint","IMPRINT",EDGE,{"disambiguationData":[TD([[subQ2,-1.0]])],"derivedFrom":subQ1}),-1.0]])]});}
            var Q121;
            {var subQ5=sQuery(id+"F0.wireOp",EDGE,"E122.13.0.3");Q121=makeQuery(id+"F0.imprint","IMPRINT",FACE,{"disambiguationData":[TD([[makeQuery(id+"F0.imprint","IMPRINT",EDGE,{"derivedFrom":subQ5}),-1.0]])]});}
            var Q122;
            {var subQ5=sQuery(id+"F0.wireOp",EDGE,"E122.12.0.3");Q122=makeQuery(id+"F0.imprint","IMPRINT",FACE,{"disambiguationData":[TD([[makeQuery(id+"F0.imprint","IMPRINT",EDGE,{"derivedFrom":subQ5}),-1.0]])]});}
            var Q123;
            {var subQ0=sQuery(id+"F0.wireOp",EDGE,"E122.12.0.2");var subQ1=sQuery(id+"F0.wireOp",EDGE,"E110");var subQ2=makeQuery(id+"F0.imprint","INTERSECT",VERTEX,{"derivedFrom":[subQ1,subQ0]});Q123=makeQuery(id+"F0.imprint","IMPRINT",FACE,{"disambiguationData":[TD([[makeQuery(id+"F0.imprint","IMPRINT",EDGE,{"disambiguationData":[TD([[subQ2,-1.0]])],"derivedFrom":subQ1}),-1.0]])]});}
            var Q124;
            {var subQ0=sQuery(id+"F0.wireOp",EDGE,"E122.11.0.2");var subQ1=sQuery(id+"F0.wireOp",EDGE,"E110");var subQ2=makeQuery(id+"F0.imprint","INTERSECT",VERTEX,{"derivedFrom":[subQ1,subQ0]});Q124=makeQuery(id+"F0.imprint","IMPRINT",FACE,{"disambiguationData":[TD([[makeQuery(id+"F0.imprint","IMPRINT",EDGE,{"disambiguationData":[TD([[subQ2,-1.0]])],"derivedFrom":subQ1}),-1.0]])]});}
            var Q125;
            {var subQ5=sQuery(id+"F0.wireOp",EDGE,"E122.11.0.3");Q125=makeQuery(id+"F0.imprint","IMPRINT",FACE,{"disambiguationData":[TD([[makeQuery(id+"F0.imprint","IMPRINT",EDGE,{"derivedFrom":subQ5}),-1.0]])]});}
            var Q126;
            {var subQ5=sQuery(id+"F0.wireOp",EDGE,"E122.10.0.3");Q126=makeQuery(id+"F0.imprint","IMPRINT",FACE,{"disambiguationData":[TD([[makeQuery(id+"F0.imprint","IMPRINT",EDGE,{"derivedFrom":subQ5}),-1.0]])]});}
            var Q127;
            {var subQ0=sQuery(id+"F0.wireOp",EDGE,"E122.10.0.2");var subQ1=sQuery(id+"F0.wireOp",EDGE,"E110");var subQ2=makeQuery(id+"F0.imprint","INTERSECT",VERTEX,{"derivedFrom":[subQ1,subQ0]});Q127=makeQuery(id+"F0.imprint","IMPRINT",FACE,{"disambiguationData":[TD([[makeQuery(id+"F0.imprint","IMPRINT",EDGE,{"disambiguationData":[TD([[subQ2,-1.0]])],"derivedFrom":subQ1}),-1.0]])]});}
            var Q128;
            {var subQ0=sQuery(id+"F0.wireOp",EDGE,"E122.9.0.2");var subQ1=sQuery(id+"F0.wireOp",EDGE,"E110");var subQ2=makeQuery(id+"F0.imprint","INTERSECT",VERTEX,{"derivedFrom":[subQ1,subQ0]});Q128=makeQuery(id+"F0.imprint","IMPRINT",FACE,{"disambiguationData":[TD([[makeQuery(id+"F0.imprint","IMPRINT",EDGE,{"disambiguationData":[TD([[subQ2,-1.0]])],"derivedFrom":subQ1}),-1.0]])]});}
            var Q129;
            {var subQ5=sQuery(id+"F0.wireOp",EDGE,"E122.9.0.3");Q129=makeQuery(id+"F0.imprint","IMPRINT",FACE,{"disambiguationData":[TD([[makeQuery(id+"F0.imprint","IMPRINT",EDGE,{"derivedFrom":subQ5}),-1.0]])]});}
            var Q130;
            {var subQ0=sQuery(id+"F0.wireOp",EDGE,"E122.8.0.2");var subQ1=sQuery(id+"F0.wireOp",EDGE,"E110");var subQ2=makeQuery(id+"F0.imprint","INTERSECT",VERTEX,{"derivedFrom":[subQ1,subQ0]});Q130=makeQuery(id+"F0.imprint","IMPRINT",FACE,{"disambiguationData":[TD([[makeQuery(id+"F0.imprint","IMPRINT",EDGE,{"disambiguationData":[TD([[subQ2,-1.0]])],"derivedFrom":subQ1}),-1.0]])]});}
            var Q131;
            {var subQ5=sQuery(id+"F0.wireOp",EDGE,"E122.8.0.3");Q131=makeQuery(id+"F0.imprint","IMPRINT",FACE,{"disambiguationData":[TD([[makeQuery(id+"F0.imprint","IMPRINT",EDGE,{"derivedFrom":subQ5}),-1.0]])]});}
            var Q132;
            {var subQ0=sQuery(id+"F0.wireOp",EDGE,"E122.7.0.2");var subQ1=sQuery(id+"F0.wireOp",EDGE,"E110");var subQ2=makeQuery(id+"F0.imprint","INTERSECT",VERTEX,{"derivedFrom":[subQ1,subQ0]});Q132=makeQuery(id+"F0.imprint","IMPRINT",FACE,{"disambiguationData":[TD([[makeQuery(id+"F0.imprint","IMPRINT",EDGE,{"disambiguationData":[TD([[subQ2,-1.0]])],"derivedFrom":subQ1}),-1.0]])]});}
            var Q133;
            {var subQ5=sQuery(id+"F0.wireOp",EDGE,"E122.7.0.3");Q133=makeQuery(id+"F0.imprint","IMPRINT",FACE,{"disambiguationData":[TD([[makeQuery(id+"F0.imprint","IMPRINT",EDGE,{"derivedFrom":subQ5}),-1.0]])]});}
            var Q134;
            {var subQ0=sQuery(id+"F0.wireOp",EDGE,"E122.6.0.2");var subQ1=sQuery(id+"F0.wireOp",EDGE,"E110");var subQ2=makeQuery(id+"F0.imprint","INTERSECT",VERTEX,{"derivedFrom":[subQ1,subQ0]});Q134=makeQuery(id+"F0.imprint","IMPRINT",FACE,{"disambiguationData":[TD([[makeQuery(id+"F0.imprint","IMPRINT",EDGE,{"disambiguationData":[TD([[subQ2,-1.0]])],"derivedFrom":subQ1}),-1.0]])]});}
            var Q135;
            {var subQ5=sQuery(id+"F0.wireOp",EDGE,"E122.6.0.3");Q135=makeQuery(id+"F0.imprint","IMPRINT",FACE,{"disambiguationData":[TD([[makeQuery(id+"F0.imprint","IMPRINT",EDGE,{"derivedFrom":subQ5}),-1.0]])]});}
            var Q136;
            {var subQ0=sQuery(id+"F0.wireOp",EDGE,"E122.5.0.2");var subQ1=sQuery(id+"F0.wireOp",EDGE,"E110");var subQ2=makeQuery(id+"F0.imprint","INTERSECT",VERTEX,{"derivedFrom":[subQ1,subQ0]});Q136=makeQuery(id+"F0.imprint","IMPRINT",FACE,{"disambiguationData":[TD([[makeQuery(id+"F0.imprint","IMPRINT",EDGE,{"disambiguationData":[TD([[subQ2,-1.0]])],"derivedFrom":subQ1}),-1.0]])]});}
            var Q137;
            {var subQ5=sQuery(id+"F0.wireOp",EDGE,"E122.5.0.3");Q137=makeQuery(id+"F0.imprint","IMPRINT",FACE,{"disambiguationData":[TD([[makeQuery(id+"F0.imprint","IMPRINT",EDGE,{"derivedFrom":subQ5}),-1.0]])]});}
            var Q138;
            {var subQ0=sQuery(id+"F0.wireOp",EDGE,"E122.4.0.2");var subQ1=sQuery(id+"F0.wireOp",EDGE,"E110");var subQ2=makeQuery(id+"F0.imprint","INTERSECT",VERTEX,{"derivedFrom":[subQ1,subQ0]});Q138=makeQuery(id+"F0.imprint","IMPRINT",FACE,{"disambiguationData":[TD([[makeQuery(id+"F0.imprint","IMPRINT",EDGE,{"disambiguationData":[TD([[subQ2,-1.0]])],"derivedFrom":subQ1}),-1.0]])]});}
            var Q139;
            {var subQ5=sQuery(id+"F0.wireOp",EDGE,"E122.4.0.3");Q139=makeQuery(id+"F0.imprint","IMPRINT",FACE,{"disambiguationData":[TD([[makeQuery(id+"F0.imprint","IMPRINT",EDGE,{"derivedFrom":subQ5}),-1.0]])]});}
            var Q140;
            {var subQ5=sQuery(id+"F0.wireOp",EDGE,"E144");Q140=makeQuery(id+"F0.imprint","IMPRINT",FACE,{"disambiguationData":[TD([[makeQuery(id+"F0.imprint","IMPRINT",EDGE,{"derivedFrom":subQ5}),1.0]])]});}
            var Q141;
            {var subQ0=sQuery(id+"F0.wireOp",EDGE,"E122.3.0.2");var subQ1=sQuery(id+"F0.wireOp",EDGE,"E110");var subQ2=makeQuery(id+"F0.imprint","INTERSECT",VERTEX,{"derivedFrom":[subQ1,subQ0]});Q141=makeQuery(id+"F0.imprint","IMPRINT",FACE,{"disambiguationData":[TD([[makeQuery(id+"F0.imprint","IMPRINT",EDGE,{"disambiguationData":[TD([[subQ2,-1.0]])],"derivedFrom":subQ1}),-1.0]])]});}
            var Q142;
            {var subQ5=sQuery(id+"F0.wireOp",EDGE,"E122.3.0.3");Q142=makeQuery(id+"F0.imprint","IMPRINT",FACE,{"disambiguationData":[TD([[makeQuery(id+"F0.imprint","IMPRINT",EDGE,{"derivedFrom":subQ5}),-1.0]])]});}
            var Q143;
            {var subQ0=sQuery(id+"F0.wireOp",EDGE,"E122.2.0.2");var subQ1=sQuery(id+"F0.wireOp",EDGE,"E110");var subQ2=makeQuery(id+"F0.imprint","INTERSECT",VERTEX,{"derivedFrom":[subQ1,subQ0]});Q143=makeQuery(id+"F0.imprint","IMPRINT",FACE,{"disambiguationData":[TD([[makeQuery(id+"F0.imprint","IMPRINT",EDGE,{"disambiguationData":[TD([[subQ2,-1.0]])],"derivedFrom":subQ1}),-1.0]])]});}
            var Q144;
            {var subQ5=sQuery(id+"F0.wireOp",EDGE,"E122.2.0.3");Q144=makeQuery(id+"F0.imprint","IMPRINT",FACE,{"disambiguationData":[TD([[makeQuery(id+"F0.imprint","IMPRINT",EDGE,{"derivedFrom":subQ5}),-1.0]])]});}
            var Q145;
            {var subQ0=sQuery(id+"F0.wireOp",EDGE,"E122.1.0.2");var subQ1=sQuery(id+"F0.wireOp",EDGE,"E110");var subQ2=makeQuery(id+"F0.imprint","INTERSECT",VERTEX,{"derivedFrom":[subQ1,subQ0]});Q145=makeQuery(id+"F0.imprint","IMPRINT",FACE,{"disambiguationData":[TD([[makeQuery(id+"F0.imprint","IMPRINT",EDGE,{"disambiguationData":[TD([[subQ2,-1.0]])],"derivedFrom":subQ1}),-1.0]])]});}
            var Q146;
            {var subQ5=sQuery(id+"F0.wireOp",EDGE,"E122.1.0.3");Q146=makeQuery(id+"F0.imprint","IMPRINT",FACE,{"disambiguationData":[TD([[makeQuery(id+"F0.imprint","IMPRINT",EDGE,{"derivedFrom":subQ5}),-1.0]])]});}
            var Q147;
            {var subQ5=sQuery(id+"F0.wireOp",EDGE,"E120");Q147=makeQuery(id+"F0.imprint","IMPRINT",FACE,{"disambiguationData":[TD([[makeQuery(id+"F0.imprint","IMPRINT",EDGE,{"derivedFrom":subQ5}),-1.0]])]});}
            var Q148;
            {var subQ0=sQuery(id+"F0.wireOp",EDGE,"E113");Q148=makeQuery(id+"F0.imprint","IMPRINT",FACE,{"disambiguationData":[TD([[makeQuery(id+"F0.imprint","IMPRINT",EDGE,{"derivedFrom":subQ0}),-1.0]])]});}
            var Q149;
            {var subQ0=sQuery(id+"F0.wireOp",EDGE,"E119");var subQ1=sQuery(id+"F0.wireOp",EDGE,"E110");var subQ2=makeQuery(id+"F0.imprint","INTERSECT",VERTEX,{"derivedFrom":[subQ1,subQ0]});Q149=makeQuery(id+"F0.imprint","IMPRINT",FACE,{"disambiguationData":[TD([[makeQuery(id+"F0.imprint","IMPRINT",EDGE,{"disambiguationData":[TD([[subQ2,-1.0]])],"derivedFrom":subQ1}),-1.0]])]});}
            var Q150;
            {var subQ0=sQuery(id+"F0.wireOp",EDGE,"E122.1.0.0");var subQ1=sQuery(id+"F0.wireOp",EDGE,"E110");var subQ2=makeQuery(id+"F0.imprint","INTERSECT",VERTEX,{"derivedFrom":[subQ1,subQ0]});Q150=makeQuery(id+"F0.imprint","IMPRINT",FACE,{"disambiguationData":[TD([[makeQuery(id+"F0.imprint","IMPRINT",EDGE,{"disambiguationData":[TD([[subQ2,-1.0]])],"derivedFrom":subQ1}),-1.0]])]});}
            var Q151;
            {var subQ0=sQuery(id+"F0.wireOp",EDGE,"E122.2.0.0");var subQ1=sQuery(id+"F0.wireOp",EDGE,"E110");var subQ2=makeQuery(id+"F0.imprint","INTERSECT",VERTEX,{"derivedFrom":[subQ1,subQ0]});Q151=makeQuery(id+"F0.imprint","IMPRINT",FACE,{"disambiguationData":[TD([[makeQuery(id+"F0.imprint","IMPRINT",EDGE,{"disambiguationData":[TD([[subQ2,-1.0]])],"derivedFrom":subQ1}),-1.0]])]});}
            var Q152;
            {var subQ0=sQuery(id+"F0.wireOp",EDGE,"E122.3.0.0");var subQ1=sQuery(id+"F0.wireOp",EDGE,"E110");var subQ2=makeQuery(id+"F0.imprint","INTERSECT",VERTEX,{"derivedFrom":[subQ1,subQ0]});Q152=makeQuery(id+"F0.imprint","IMPRINT",FACE,{"disambiguationData":[TD([[makeQuery(id+"F0.imprint","IMPRINT",EDGE,{"disambiguationData":[TD([[subQ2,-1.0]])],"derivedFrom":subQ1}),-1.0]])]});}
            var Q153;
            {var subQ0=sQuery(id+"F0.wireOp",EDGE,"E122.4.0.0");var subQ1=sQuery(id+"F0.wireOp",EDGE,"E110");var subQ2=makeQuery(id+"F0.imprint","INTERSECT",VERTEX,{"derivedFrom":[subQ1,subQ0]});Q153=makeQuery(id+"F0.imprint","IMPRINT",FACE,{"disambiguationData":[TD([[makeQuery(id+"F0.imprint","IMPRINT",EDGE,{"disambiguationData":[TD([[subQ2,-1.0]])],"derivedFrom":subQ1}),-1.0]])]});}
            var Q154;
            {var subQ0=sQuery(id+"F0.wireOp",EDGE,"E122.5.0.0");var subQ1=sQuery(id+"F0.wireOp",EDGE,"E110");var subQ2=makeQuery(id+"F0.imprint","INTERSECT",VERTEX,{"derivedFrom":[subQ1,subQ0]});Q154=makeQuery(id+"F0.imprint","IMPRINT",FACE,{"disambiguationData":[TD([[makeQuery(id+"F0.imprint","IMPRINT",EDGE,{"disambiguationData":[TD([[subQ2,-1.0]])],"derivedFrom":subQ1}),-1.0]])]});}
            var Q155;
            {var subQ0=sQuery(id+"F0.wireOp",EDGE,"E122.6.0.0");var subQ1=sQuery(id+"F0.wireOp",EDGE,"E110");var subQ2=makeQuery(id+"F0.imprint","INTERSECT",VERTEX,{"derivedFrom":[subQ1,subQ0]});Q155=makeQuery(id+"F0.imprint","IMPRINT",FACE,{"disambiguationData":[TD([[makeQuery(id+"F0.imprint","IMPRINT",EDGE,{"disambiguationData":[TD([[subQ2,-1.0]])],"derivedFrom":subQ1}),-1.0]])]});}
            var Q156;
            {var subQ0=sQuery(id+"F0.wireOp",EDGE,"E122.7.0.0");var subQ1=sQuery(id+"F0.wireOp",EDGE,"E110");var subQ2=makeQuery(id+"F0.imprint","INTERSECT",VERTEX,{"derivedFrom":[subQ1,subQ0]});Q156=makeQuery(id+"F0.imprint","IMPRINT",FACE,{"disambiguationData":[TD([[makeQuery(id+"F0.imprint","IMPRINT",EDGE,{"disambiguationData":[TD([[subQ2,-1.0]])],"derivedFrom":subQ1}),-1.0]])]});}
            var Q157;
            {var subQ0=sQuery(id+"F0.wireOp",EDGE,"E122.8.0.0");var subQ1=sQuery(id+"F0.wireOp",EDGE,"E110");var subQ2=makeQuery(id+"F0.imprint","INTERSECT",VERTEX,{"derivedFrom":[subQ1,subQ0]});Q157=makeQuery(id+"F0.imprint","IMPRINT",FACE,{"disambiguationData":[TD([[makeQuery(id+"F0.imprint","IMPRINT",EDGE,{"disambiguationData":[TD([[subQ2,-1.0]])],"derivedFrom":subQ1}),-1.0]])]});}
            var Q158;
            {var subQ0=sQuery(id+"F0.wireOp",EDGE,"E122.9.0.0");var subQ1=sQuery(id+"F0.wireOp",EDGE,"E110");var subQ2=makeQuery(id+"F0.imprint","INTERSECT",VERTEX,{"derivedFrom":[subQ1,subQ0]});Q158=makeQuery(id+"F0.imprint","IMPRINT",FACE,{"disambiguationData":[TD([[makeQuery(id+"F0.imprint","IMPRINT",EDGE,{"disambiguationData":[TD([[subQ2,-1.0]])],"derivedFrom":subQ1}),-1.0]])]});}
            var Q159;
            {var subQ0=sQuery(id+"F0.wireOp",EDGE,"E122.10.0.0");var subQ1=sQuery(id+"F0.wireOp",EDGE,"E110");var subQ2=makeQuery(id+"F0.imprint","INTERSECT",VERTEX,{"derivedFrom":[subQ1,subQ0]});Q159=makeQuery(id+"F0.imprint","IMPRINT",FACE,{"disambiguationData":[TD([[makeQuery(id+"F0.imprint","IMPRINT",EDGE,{"disambiguationData":[TD([[subQ2,-1.0]])],"derivedFrom":subQ1}),-1.0]])]});}
            var Q160;
            {var subQ0=sQuery(id+"F0.wireOp",EDGE,"E122.11.0.0");var subQ1=sQuery(id+"F0.wireOp",EDGE,"E110");var subQ2=makeQuery(id+"F0.imprint","INTERSECT",VERTEX,{"derivedFrom":[subQ1,subQ0]});Q160=makeQuery(id+"F0.imprint","IMPRINT",FACE,{"disambiguationData":[TD([[makeQuery(id+"F0.imprint","IMPRINT",EDGE,{"disambiguationData":[TD([[subQ2,-1.0]])],"derivedFrom":subQ1}),-1.0]])]});}
            var Q161;
            {var subQ0=sQuery(id+"F0.wireOp",EDGE,"E122.12.0.0");var subQ1=sQuery(id+"F0.wireOp",EDGE,"E110");var subQ2=makeQuery(id+"F0.imprint","INTERSECT",VERTEX,{"derivedFrom":[subQ1,subQ0]});Q161=makeQuery(id+"F0.imprint","IMPRINT",FACE,{"disambiguationData":[TD([[makeQuery(id+"F0.imprint","IMPRINT",EDGE,{"disambiguationData":[TD([[subQ2,-1.0]])],"derivedFrom":subQ1}),-1.0]])]});}
            var Q162;
            {var subQ0=sQuery(id+"F0.wireOp",EDGE,"E122.13.0.0");var subQ1=sQuery(id+"F0.wireOp",EDGE,"E110");var subQ2=makeQuery(id+"F0.imprint","INTERSECT",VERTEX,{"derivedFrom":[subQ1,subQ0]});Q162=makeQuery(id+"F0.imprint","IMPRINT",FACE,{"disambiguationData":[TD([[makeQuery(id+"F0.imprint","IMPRINT",EDGE,{"disambiguationData":[TD([[subQ2,-1.0]])],"derivedFrom":subQ1}),-1.0]])]});}
            var Q163;
            {var subQ0=sQuery(id+"F0.wireOp",EDGE,"E122.14.0.2");var subQ1=sQuery(id+"F0.wireOp",EDGE,"E110");var subQ2=makeQuery(id+"F0.imprint","INTERSECT",VERTEX,{"derivedFrom":[subQ1,subQ0]});Q163=makeQuery(id+"F0.imprint","IMPRINT",FACE,{"disambiguationData":[TD([[makeQuery(id+"F0.imprint","IMPRINT",EDGE,{"disambiguationData":[TD([[subQ2,-1.0]])],"derivedFrom":subQ1}),-1.0]])]});}
            var Q164;
            {var subQ0=sQuery(id+"F0.wireOp",EDGE,"E122.14.0.0");var subQ1=sQuery(id+"F0.wireOp",EDGE,"E110");var subQ2=makeQuery(id+"F0.imprint","INTERSECT",VERTEX,{"derivedFrom":[subQ1,subQ0]});Q164=makeQuery(id+"F0.imprint","IMPRINT",FACE,{"disambiguationData":[TD([[makeQuery(id+"F0.imprint","IMPRINT",EDGE,{"disambiguationData":[TD([[subQ2,-1.0]])],"derivedFrom":subQ1}),-1.0]])]});}
            var Q165;
            {var subQ0=sQuery(id+"F0.wireOp",EDGE,"E122.15.0.2");var subQ1=sQuery(id+"F0.wireOp",EDGE,"E110");var subQ2=makeQuery(id+"F0.imprint","INTERSECT",VERTEX,{"derivedFrom":[subQ1,subQ0]});Q165=makeQuery(id+"F0.imprint","IMPRINT",FACE,{"disambiguationData":[TD([[makeQuery(id+"F0.imprint","IMPRINT",EDGE,{"disambiguationData":[TD([[subQ2,-1.0]])],"derivedFrom":subQ1}),-1.0]])]});}
            var Q166;
            {var subQ0=sQuery(id+"F0.wireOp",EDGE,"E122.15.0.0");var subQ1=sQuery(id+"F0.wireOp",EDGE,"E110");var subQ2=makeQuery(id+"F0.imprint","INTERSECT",VERTEX,{"derivedFrom":[subQ1,subQ0]});Q166=makeQuery(id+"F0.imprint","IMPRINT",FACE,{"disambiguationData":[TD([[makeQuery(id+"F0.imprint","IMPRINT",EDGE,{"disambiguationData":[TD([[subQ2,-1.0]])],"derivedFrom":subQ1}),-1.0]])]});}
            var Q167;
            {var subQ0=sQuery(id+"F0.wireOp",EDGE,"E122.16.0.2");var subQ1=sQuery(id+"F0.wireOp",EDGE,"E110");var subQ2=makeQuery(id+"F0.imprint","INTERSECT",VERTEX,{"derivedFrom":[subQ1,subQ0]});Q167=makeQuery(id+"F0.imprint","IMPRINT",FACE,{"disambiguationData":[TD([[makeQuery(id+"F0.imprint","IMPRINT",EDGE,{"disambiguationData":[TD([[subQ2,-1.0]])],"derivedFrom":subQ1}),-1.0]])]});}
            var Q168;
            {var subQ0=sQuery(id+"F0.wireOp",EDGE,"E122.16.0.0");var subQ1=sQuery(id+"F0.wireOp",EDGE,"E110");var subQ2=makeQuery(id+"F0.imprint","INTERSECT",VERTEX,{"derivedFrom":[subQ1,subQ0]});Q168=makeQuery(id+"F0.imprint","IMPRINT",FACE,{"disambiguationData":[TD([[makeQuery(id+"F0.imprint","IMPRINT",EDGE,{"disambiguationData":[TD([[subQ2,-1.0]])],"derivedFrom":subQ1}),-1.0]])]});}
            var Q169;
            {var subQ0=sQuery(id+"F0.wireOp",EDGE,"E122.17.0.2");var subQ1=sQuery(id+"F0.wireOp",EDGE,"E110");var subQ2=makeQuery(id+"F0.imprint","INTERSECT",VERTEX,{"derivedFrom":[subQ1,subQ0]});Q169=makeQuery(id+"F0.imprint","IMPRINT",FACE,{"disambiguationData":[TD([[makeQuery(id+"F0.imprint","IMPRINT",EDGE,{"disambiguationData":[TD([[subQ2,-1.0]])],"derivedFrom":subQ1}),-1.0]])]});}
            var Q170;
            {var subQ0=sQuery(id+"F0.wireOp",EDGE,"E122.17.0.0");var subQ1=sQuery(id+"F0.wireOp",EDGE,"E110");var subQ2=makeQuery(id+"F0.imprint","INTERSECT",VERTEX,{"derivedFrom":[subQ1,subQ0]});Q170=makeQuery(id+"F0.imprint","IMPRINT",FACE,{"disambiguationData":[TD([[makeQuery(id+"F0.imprint","IMPRINT",EDGE,{"disambiguationData":[TD([[subQ2,-1.0]])],"derivedFrom":subQ1}),-1.0]])]});}
            var Q171;
            {var subQ0=sQuery(id+"F0.wireOp",EDGE,"E122.18.0.2");var subQ1=sQuery(id+"F0.wireOp",EDGE,"E110");var subQ2=makeQuery(id+"F0.imprint","INTERSECT",VERTEX,{"derivedFrom":[subQ1,subQ0]});Q171=makeQuery(id+"F0.imprint","IMPRINT",FACE,{"disambiguationData":[TD([[makeQuery(id+"F0.imprint","IMPRINT",EDGE,{"disambiguationData":[TD([[subQ2,-1.0]])],"derivedFrom":subQ1}),-1.0]])]});}
            var Q172;
            {var subQ0=sQuery(id+"F0.wireOp",EDGE,"E122.18.0.0");var subQ1=sQuery(id+"F0.wireOp",EDGE,"E110");var subQ2=makeQuery(id+"F0.imprint","INTERSECT",VERTEX,{"derivedFrom":[subQ1,subQ0]});Q172=makeQuery(id+"F0.imprint","IMPRINT",FACE,{"disambiguationData":[TD([[makeQuery(id+"F0.imprint","IMPRINT",EDGE,{"disambiguationData":[TD([[subQ2,-1.0]])],"derivedFrom":subQ1}),-1.0]])]});}
            var Q173;
            {var subQ0=sQuery(id+"F0.wireOp",EDGE,"E122.19.0.2");var subQ1=sQuery(id+"F0.wireOp",EDGE,"E110");var subQ2=makeQuery(id+"F0.imprint","INTERSECT",VERTEX,{"derivedFrom":[subQ1,subQ0]});Q173=makeQuery(id+"F0.imprint","IMPRINT",FACE,{"disambiguationData":[TD([[makeQuery(id+"F0.imprint","IMPRINT",EDGE,{"disambiguationData":[TD([[subQ2,-1.0]])],"derivedFrom":subQ1}),-1.0]])]});}
            var Q174;
            {var subQ0=sQuery(id+"F0.wireOp",EDGE,"E122.19.0.0");var subQ1=sQuery(id+"F0.wireOp",EDGE,"E110");var subQ2=makeQuery(id+"F0.imprint","INTERSECT",VERTEX,{"derivedFrom":[subQ1,subQ0]});Q174=makeQuery(id+"F0.imprint","IMPRINT",FACE,{"disambiguationData":[TD([[makeQuery(id+"F0.imprint","IMPRINT",EDGE,{"disambiguationData":[TD([[subQ2,-1.0]])],"derivedFrom":subQ1}),-1.0]])]});}
            var Q175;
            {var subQ0=sQuery(id+"F0.wireOp",EDGE,"E122.20.0.2");var subQ1=sQuery(id+"F0.wireOp",EDGE,"E110");var subQ2=makeQuery(id+"F0.imprint","INTERSECT",VERTEX,{"derivedFrom":[subQ1,subQ0]});Q175=makeQuery(id+"F0.imprint","IMPRINT",FACE,{"disambiguationData":[TD([[makeQuery(id+"F0.imprint","IMPRINT",EDGE,{"disambiguationData":[TD([[subQ2,-1.0]])],"derivedFrom":subQ1}),-1.0]])]});}
            var Q176;
            {var subQ0=sQuery(id+"F0.wireOp",EDGE,"E122.20.0.0");var subQ1=sQuery(id+"F0.wireOp",EDGE,"E110");var subQ2=makeQuery(id+"F0.imprint","INTERSECT",VERTEX,{"derivedFrom":[subQ1,subQ0]});Q176=makeQuery(id+"F0.imprint","IMPRINT",FACE,{"disambiguationData":[TD([[makeQuery(id+"F0.imprint","IMPRINT",EDGE,{"disambiguationData":[TD([[subQ2,-1.0]])],"derivedFrom":subQ1}),-1.0]])]});}
            var Q177;
            {var subQ5=sQuery(id+"F0.wireOp",EDGE,"E122.25.0.3");Q177=makeQuery(id+"F0.imprint","IMPRINT",FACE,{"disambiguationData":[TD([[makeQuery(id+"F0.imprint","IMPRINT",EDGE,{"derivedFrom":subQ5}),-1.0]])]});}
            var Q178;
            {var subQ5=sQuery(id+"F0.wireOp",EDGE,"E122.24.0.3");Q178=makeQuery(id+"F0.imprint","IMPRINT",FACE,{"disambiguationData":[TD([[makeQuery(id+"F0.imprint","IMPRINT",EDGE,{"derivedFrom":subQ5}),-1.0]])]});}
            var Q179;
            {var subQ5=sQuery(id+"F0.wireOp",EDGE,"E122.23.0.3");Q179=makeQuery(id+"F0.imprint","IMPRINT",FACE,{"disambiguationData":[TD([[makeQuery(id+"F0.imprint","IMPRINT",EDGE,{"derivedFrom":subQ5}),-1.0]])]});}
            var Q180;
            {var subQ5=sQuery(id+"F0.wireOp",EDGE,"E122.22.0.3");Q180=makeQuery(id+"F0.imprint","IMPRINT",FACE,{"disambiguationData":[TD([[makeQuery(id+"F0.imprint","IMPRINT",EDGE,{"derivedFrom":subQ5}),-1.0]])]});}
            var Q181;
            {var subQ5=sQuery(id+"F0.wireOp",EDGE,"E122.21.0.3");Q181=makeQuery(id+"F0.imprint","IMPRINT",FACE,{"disambiguationData":[TD([[makeQuery(id+"F0.imprint","IMPRINT",EDGE,{"derivedFrom":subQ5}),-1.0]])]});}
            var Q182;
            {var subQ5=sQuery(id+"F0.wireOp",EDGE,"E122.20.0.3");Q182=makeQuery(id+"F0.imprint","IMPRINT",FACE,{"disambiguationData":[TD([[makeQuery(id+"F0.imprint","IMPRINT",EDGE,{"derivedFrom":subQ5}),-1.0]])]});}
            var Q183;
            {var subQ5=sQuery(id+"F0.wireOp",EDGE,"E122.19.0.3");Q183=makeQuery(id+"F0.imprint","IMPRINT",FACE,{"disambiguationData":[TD([[makeQuery(id+"F0.imprint","IMPRINT",EDGE,{"derivedFrom":subQ5}),-1.0]])]});}
            var Q184;
            {var subQ5=sQuery(id+"F0.wireOp",EDGE,"E122.18.0.3");Q184=makeQuery(id+"F0.imprint","IMPRINT",FACE,{"disambiguationData":[TD([[makeQuery(id+"F0.imprint","IMPRINT",EDGE,{"derivedFrom":subQ5}),-1.0]])]});}
            var Q185;
            {var subQ5=sQuery(id+"F0.wireOp",EDGE,"E122.17.0.3");Q185=makeQuery(id+"F0.imprint","IMPRINT",FACE,{"disambiguationData":[TD([[makeQuery(id+"F0.imprint","IMPRINT",EDGE,{"derivedFrom":subQ5}),-1.0]])]});}
            var Q186;
            {var subQ5=sQuery(id+"F0.wireOp",EDGE,"E122.16.0.3");Q186=makeQuery(id+"F0.imprint","IMPRINT",FACE,{"disambiguationData":[TD([[makeQuery(id+"F0.imprint","IMPRINT",EDGE,{"derivedFrom":subQ5}),-1.0]])]});}
            var Q187;
            {var subQ5=sQuery(id+"F0.wireOp",EDGE,"E122.15.0.3");Q187=makeQuery(id+"F0.imprint","IMPRINT",FACE,{"disambiguationData":[TD([[makeQuery(id+"F0.imprint","IMPRINT",EDGE,{"derivedFrom":subQ5}),-1.0]])]});}
            var Q188;
            {var subQ5=sQuery(id+"F0.wireOp",EDGE,"E122.14.0.3");Q188=makeQuery(id+"F0.imprint","IMPRINT",FACE,{"disambiguationData":[TD([[makeQuery(id+"F0.imprint","IMPRINT",EDGE,{"derivedFrom":subQ5}),-1.0]])]});}
            extrude(context, id + "F1", {"entities" : qUnion([Q0, Q1, Q2, Q3, Q4, Q5, Q6, Q7, Q8, Q9, Q10, Q11, Q12, Q13, Q14, Q15, Q16, Q17, Q18, Q19, Q20, Q21, Q22, Q23, Q24, Q25, Q26, Q27, Q28, Q29, Q30, Q31, Q32, Q33, Q34, Q35, Q36, Q37, Q38, Q39, Q40, Q41, Q42, Q43, Q44, Q45, Q46, Q47, Q48, Q49, Q50, Q51, Q52, Q53, Q54, Q55, Q56, Q57, Q58, Q59, Q60, Q61, Q62, Q63, Q64, Q65, Q66, Q67, Q68, Q69, Q70, Q71, Q72, Q73, Q74, Q75, Q76, Q77, Q78, Q79, Q80, Q81, Q82, Q83, Q84, Q85, Q86, Q87, Q88, Q89, Q90, Q91, Q92, Q93, Q94, Q95, Q96, Q97, Q98, Q99, Q100, Q101, Q102, Q103, Q104, Q105, Q106, Q107, Q108, Q109, Q110, Q111, Q112, Q113, Q114, Q115, Q116, Q117, Q118, Q119, Q120, Q121, Q122, Q123, Q124, Q125, Q126, Q127, Q128, Q129, Q130, Q131, Q132, Q133, Q134, Q135, Q136, Q137, Q138, Q139, Q140, Q141, Q142, Q143, Q144, Q145, Q146, Q147, Q148, Q149, Q150, Q151, Q152, Q153, Q154, Q155, Q156, Q157, Q158, Q159, Q160, Q161, Q162, Q163, Q164, Q165, Q166, Q167, Q168, Q169, Q170, Q171, Q172, Q173, Q174, Q175, Q176, Q177, Q178, Q179, Q180, Q181, Q182, Q183, Q184, Q185, Q186, Q187, Q188]), "depth" : 25 * mm});
        }
    });
